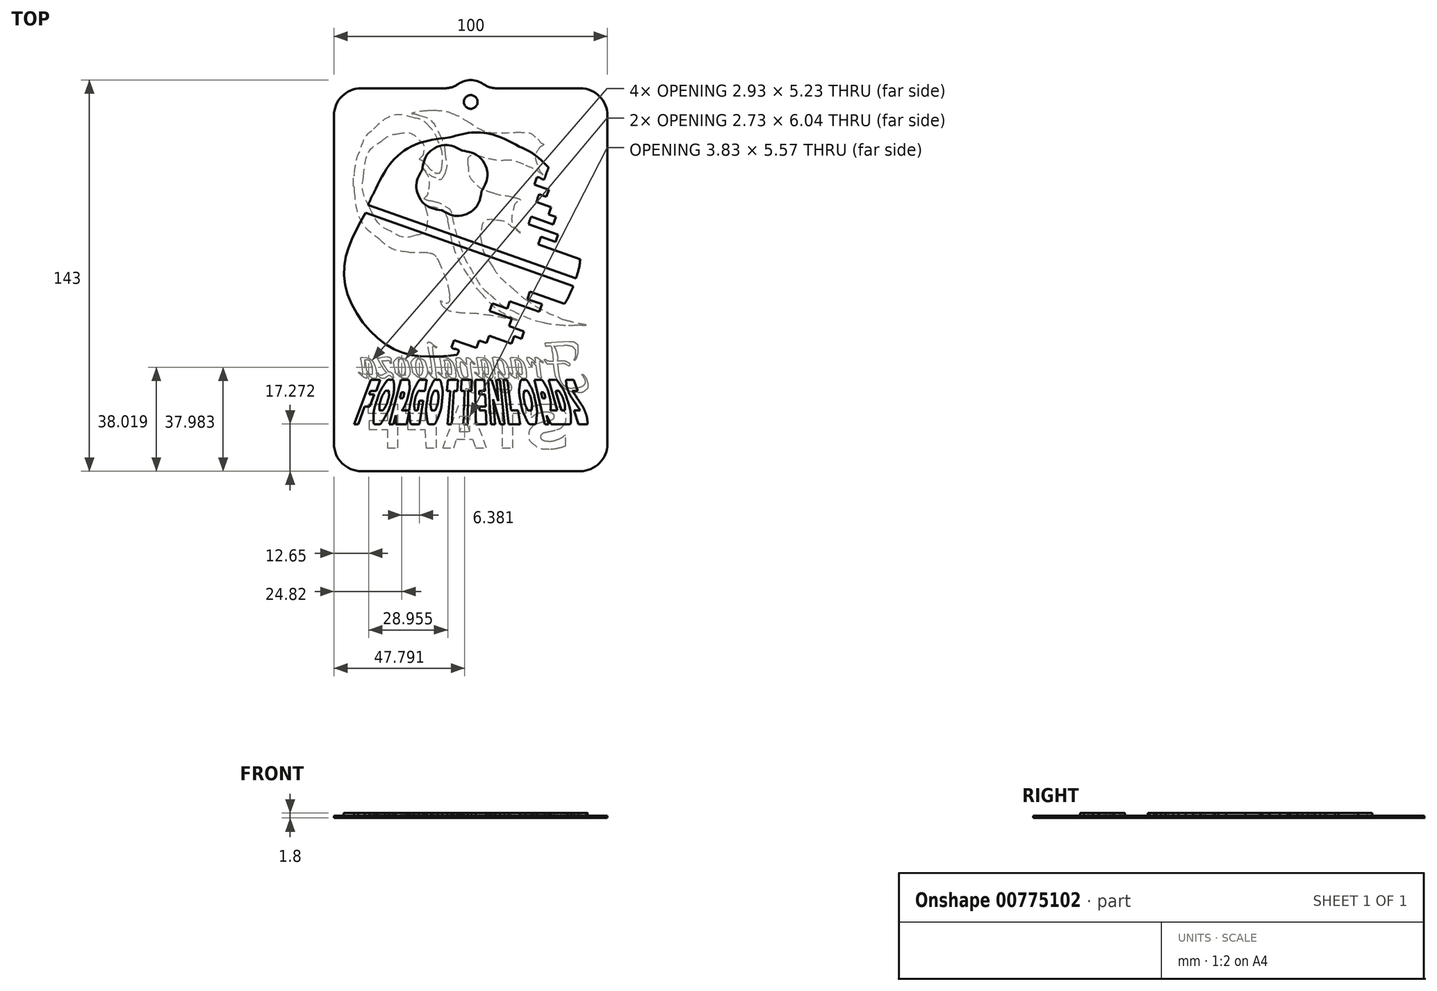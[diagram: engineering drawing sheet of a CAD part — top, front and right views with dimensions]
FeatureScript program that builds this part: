
annotation { "Feature Type Name" : "Feature", "Feature Type Description" : "" }
export const myFeature = defineFeature(function(context is Context, id is Id, definition is map)
    precondition{}
    {
        {
            var Q0;
            Q0=qCreatedBy(makeId("Top.planeOp"),FACE);
            var sketch = newSketch(context, id + "F0", { "sketchPlane" : qUnion([Q0])});
            skLineSegment(sketch, "E0.bottom", {"start": v(-40, 70) * mm, "end": v(-9.33, 70) * mm});
            skLineSegment(sketch, "E0.top", {"start": v(-40, -70) * mm, "end": v(40, -70) * mm});
            skLineSegment(sketch, "E0.left", {"start": v(-50, 60) * mm, "end": v(-50, -60) * mm});
            skLineSegment(sketch, "E0.right", {"start": v(50, 60) * mm, "end": v(50, -60) * mm});
            skPoint(sketch, "E0.middle", {"position": v(0, 0) * mm});
            skCircle(sketch, "E1", {"center": v(0, 65) * mm, "radius": 2.5 * mm});
            skPoint(sketch, "E2.visualSharp", {"position": v(-50, 70) * mm});
            skArc(sketch, "E2.filletArc", {"start": v(-40, 70) * mm, "mid": v(-47.07, 67.07) * mm, "end": v(-50, 60) * mm});
            skPoint(sketch, "E3.visualSharp", {"position": v(50, 70) * mm});
            skArc(sketch, "E3.filletArc", {"start": v(50, 60) * mm, "mid": v(47.07, 67.07) * mm, "end": v(40, 70) * mm});
            skPoint(sketch, "E4.visualSharp", {"position": v(50, -70) * mm});
            skArc(sketch, "E4.filletArc", {"start": v(40, -70) * mm, "mid": v(47.07, -67.07) * mm, "end": v(50, -60) * mm});
            skPoint(sketch, "E5.visualSharp", {"position": v(-50, -70) * mm});
            skArc(sketch, "E5.filletArc", {"start": v(-50, -60) * mm, "mid": v(-47.07, -67.07) * mm, "end": v(-40, -70) * mm});
            skArc(sketch, "E6", {"start": v(-4.66, 71.5) * mm, "mid": v(0, 73) * mm, "end": v(4.66, 71.5) * mm});
            skArc(sketch, "E7.filletArc", {"start": v(-9.33, 70) * mm, "mid": v(-6.88, 70.38) * mm, "end": v(-4.66, 71.5) * mm});
            skLineSegment(sketch, "E8", {"start": v(40, 70) * mm, "end": v(9.33, 70) * mm});
            skArc(sketch, "E9.filletArc", {"start": v(4.66, 71.5) * mm, "mid": v(6.88, 70.38) * mm, "end": v(9.33, 70) * mm});
            skSolve(sketch);
        }
        {
            var Q0;
            Q0=qCreatedBy(makeId("Top.planeOp"),FACE);
            var sketch = newSketch(context, id + "F1", { "sketchPlane" : qUnion([Q0])});
            skLineSegment(sketch, "E10", {"start": v(38.17, -16.7) * mm, "end": v(38.78, -16.7) * mm});
            skLineSegment(sketch, "E11", {"start": v(-13.07, 61.96) * mm, "end": v(-13.17, 61.96) * mm});
            skLineSegment(sketch, "E12", {"start": v(-14.17, 61.96) * mm, "end": v(-14.37, 61.96) * mm});
            skLineSegment(sketch, "E13", {"start": v(-42.85, 37.93) * mm, "end": v(-42.85, 36.81) * mm});
            skLineSegment(sketch, "E14", {"start": v(-42.85, 35.49) * mm, "end": v(-42.85, 34.98) * mm});
            skLineSegment(sketch, "E15", {"start": v(-42.85, 34.78) * mm, "end": v(-42.85, 34.16) * mm});
            skLineSegment(sketch, "E16", {"start": v(40.64, -16.7) * mm, "end": v(40.63, -16.62) * mm});
            skLineSegment(sketch, "E17", {"start": v(38.83, -16.7) * mm, "end": v(40.64, -16.7) * mm});
            skLineSegment(sketch, "E18", {"start": v(-42.85, 36.81) * mm, "end": v(-42.85, 35.49) * mm});
            skLineSegment(sketch, "E19", {"start": v(-13.21, 61.96) * mm, "end": v(-14.22, 61.96) * mm});
            skLineSegment(sketch, "E20", {"start": v(-42.85, 34.98) * mm, "end": v(-42.85, 34.77) * mm});
            skLineSegment(sketch, "E21", {"start": v(36.03, -31.52) * mm, "end": v(35.01, -30.98) * mm});
            skLineSegment(sketch, "E22", {"start": v(33.37, -30.7) * mm, "end": v(32.17, -30.75) * mm});
            skLineSegment(sketch, "E23", {"start": v(32.17, -30.75) * mm, "end": v(30.92, -30.82) * mm});
            skLineSegment(sketch, "E24", {"start": v(30.92, -30.82) * mm, "end": v(27.9, -30.82) * mm});
            skLineSegment(sketch, "E25", {"start": v(27.9, -30.82) * mm, "end": v(27.52, -30.26) * mm});
            skLineSegment(sketch, "E26", {"start": v(26.88, -29.35) * mm, "end": v(26.9, -29.28) * mm});
            skLineSegment(sketch, "E27", {"start": v(30.32, -29.76) * mm, "end": v(31.57, -29.76) * mm});
            skLineSegment(sketch, "E28", {"start": v(31.57, -29.76) * mm, "end": v(33.15, -29.76) * mm});
            skLineSegment(sketch, "E29", {"start": v(33.15, -29.76) * mm, "end": v(34.41, -29.76) * mm});
            skLineSegment(sketch, "E30", {"start": v(34.05, -24.06) * mm, "end": v(31.6, -24.16) * mm});
            skLineSegment(sketch, "E31", {"start": v(31.6, -24.16) * mm, "end": v(29.36, -24.3) * mm});
            skLineSegment(sketch, "E32", {"start": v(27.3, -24.39) * mm, "end": v(27.09, -23.13) * mm});
            skLineSegment(sketch, "E33", {"start": v(29.45, -22.97) * mm, "end": v(31.35, -22.93) * mm});
            skLineSegment(sketch, "E34", {"start": v(31.35, -22.93) * mm, "end": v(33.78, -22.78) * mm});
            skLineSegment(sketch, "E35", {"start": v(33.78, -22.78) * mm, "end": v(36.14, -22.66) * mm});
            skLineSegment(sketch, "E36", {"start": v(38.04, -29.5) * mm, "end": v(37.7, -29.32) * mm});
            skLineSegment(sketch, "E37", {"start": v(30.25, -30.2) * mm, "end": v(29.88, -26.54) * mm});
            skLineSegment(sketch, "E38", {"start": v(29.55, -24.56) * mm, "end": v(29.3, -24.3) * mm});
            skLineSegment(sketch, "E39", {"start": v(29.18, -23.96) * mm, "end": v(29.55, -24.04) * mm});
            skLineSegment(sketch, "E40", {"start": v(31.76, -29.06) * mm, "end": v(31.88, -31.82) * mm});
            skLineSegment(sketch, "E41", {"start": v(37.27, -39.71) * mm, "end": v(38.3, -39.63) * mm});
            skLineSegment(sketch, "E42", {"start": v(41.15, -35.4) * mm, "end": v(40.78, -34.92) * mm});
            skLineSegment(sketch, "E43", {"start": v(40.78, -34.92) * mm, "end": v(40.72, -34.76) * mm});
            skLineSegment(sketch, "E44", {"start": v(23.56, -29.53) * mm, "end": v(23.5, -28.89) * mm});
            skLineSegment(sketch, "E45", {"start": v(24.23, -28.54) * mm, "end": v(25.22, -29.23) * mm});
            skLineSegment(sketch, "E46", {"start": v(25.22, -29.23) * mm, "end": v(26.33, -30.01) * mm});
            skLineSegment(sketch, "E47", {"start": v(26.48, -30.3) * mm, "end": v(26.4, -30.34) * mm});
            skLineSegment(sketch, "E48", {"start": v(26.4, -30.34) * mm, "end": v(26.3, -30.32) * mm});
            skLineSegment(sketch, "E49", {"start": v(26.3, -30.32) * mm, "end": v(26.17, -30.3) * mm});
            skLineSegment(sketch, "E50", {"start": v(25.15, -30.3) * mm, "end": v(25.53, -33.54) * mm});
            skLineSegment(sketch, "E51", {"start": v(25.53, -33.54) * mm, "end": v(25.79, -35.64) * mm});
            skLineSegment(sketch, "E52", {"start": v(25.88, -36) * mm, "end": v(24.4, -35.44) * mm});
            skLineSegment(sketch, "E53", {"start": v(23.19, -29.85) * mm, "end": v(23.89, -30.75) * mm});
            skLineSegment(sketch, "E54", {"start": v(23.65, -31.18) * mm, "end": v(23.19, -30.77) * mm});
            skLineSegment(sketch, "E55", {"start": v(15.9, -29.4) * mm, "end": v(15.4, -29.4) * mm});
            skLineSegment(sketch, "E56", {"start": v(15.4, -29.4) * mm, "end": v(15.02, -29.33) * mm});
            skLineSegment(sketch, "E57", {"start": v(15.24, -28.42) * mm, "end": v(16.71, -28.55) * mm});
            skLineSegment(sketch, "E58", {"start": v(17.3, -34.56) * mm, "end": v(16.63, -33.84) * mm});
            skLineSegment(sketch, "E59", {"start": v(16.01, -32.3) * mm, "end": v(16.46, -32.84) * mm});
            skLineSegment(sketch, "E60", {"start": v(16.96, -29.4) * mm, "end": v(16.5, -29.4) * mm});
            skLineSegment(sketch, "E61", {"start": v(16.5, -29.4) * mm, "end": v(15.9, -29.4) * mm});
            skLineSegment(sketch, "E62", {"start": v(16.38, -31.1) * mm, "end": v(16.6, -32.79) * mm});
            skLineSegment(sketch, "E63", {"start": v(16.6, -32.79) * mm, "end": v(16.8, -34.4) * mm});
            skLineSegment(sketch, "E64", {"start": v(16.8, -34.4) * mm, "end": v(16.85, -35.3) * mm});
            skLineSegment(sketch, "E65", {"start": v(14.85, -34.45) * mm, "end": v(15.26, -34.75) * mm});
            skLineSegment(sketch, "E66", {"start": v(15.33, -34.51) * mm, "end": v(15.26, -33.72) * mm});
            skLineSegment(sketch, "E67", {"start": v(15.26, -33.72) * mm, "end": v(14.93, -31.64) * mm});
            skLineSegment(sketch, "E68", {"start": v(14.93, -31.64) * mm, "end": v(14.54, -29.14) * mm});
            skLineSegment(sketch, "E69", {"start": v(9.13, -29.4) * mm, "end": v(8.63, -29.4) * mm});
            skLineSegment(sketch, "E70", {"start": v(8.63, -29.4) * mm, "end": v(8.27, -29.31) * mm});
            skLineSegment(sketch, "E71", {"start": v(8.04, -29.08) * mm, "end": v(7.89, -28.74) * mm});
            skLineSegment(sketch, "E72", {"start": v(8.47, -28.35) * mm, "end": v(8.95, -28.35) * mm});
            skLineSegment(sketch, "E73", {"start": v(8.95, -28.35) * mm, "end": v(9.46, -28.52) * mm});
            skLineSegment(sketch, "E74", {"start": v(9.46, -28.52) * mm, "end": v(10.14, -28.6) * mm});
            skLineSegment(sketch, "E75", {"start": v(11.28, -34.74) * mm, "end": v(10.47, -33.88) * mm});
            skLineSegment(sketch, "E76", {"start": v(9.69, -32.05) * mm, "end": v(10.37, -32.95) * mm});
            skLineSegment(sketch, "E77", {"start": v(10.37, -32.95) * mm, "end": v(11.14, -33.94) * mm});
            skLineSegment(sketch, "E78", {"start": v(12.6, -34.13) * mm, "end": v(12.52, -33.32) * mm});
            skLineSegment(sketch, "E79", {"start": v(12.52, -33.32) * mm, "end": v(12.29, -32.26) * mm});
            skLineSegment(sketch, "E80", {"start": v(12.29, -32.26) * mm, "end": v(12.13, -31.6) * mm});
            skLineSegment(sketch, "E81", {"start": v(10.33, -29.4) * mm, "end": v(9.77, -29.4) * mm});
            skLineSegment(sketch, "E82", {"start": v(9.77, -29.4) * mm, "end": v(9.13, -29.4) * mm});
            skLineSegment(sketch, "E83", {"start": v(9.46, -28.84) * mm, "end": v(9.77, -30.97) * mm});
            skLineSegment(sketch, "E84", {"start": v(9.77, -30.97) * mm, "end": v(10.1, -34.04) * mm});
            skLineSegment(sketch, "E85", {"start": v(10.1, -34.04) * mm, "end": v(10.34, -36.29) * mm});
            skLineSegment(sketch, "E86", {"start": v(10.34, -36.29) * mm, "end": v(10.47, -37.68) * mm});
            skLineSegment(sketch, "E87", {"start": v(12.25, -36.7) * mm, "end": v(11.22, -36.28) * mm});
            skLineSegment(sketch, "E88", {"start": v(10.66, -36) * mm, "end": v(10.7, -35.94) * mm});
            skLineSegment(sketch, "E89", {"start": v(8.88, -35.3) * mm, "end": v(8.5, -31.75) * mm});
            skLineSegment(sketch, "E90", {"start": v(3.54, -29.4) * mm, "end": v(3.04, -29.4) * mm});
            skLineSegment(sketch, "E91", {"start": v(3.04, -29.4) * mm, "end": v(2.67, -29.33) * mm});
            skLineSegment(sketch, "E92", {"start": v(2.88, -28.42) * mm, "end": v(4.36, -28.55) * mm});
            skLineSegment(sketch, "E93", {"start": v(4.94, -34.56) * mm, "end": v(4.28, -33.84) * mm});
            skLineSegment(sketch, "E94", {"start": v(3.66, -32.3) * mm, "end": v(4.1, -32.84) * mm});
            skLineSegment(sketch, "E95", {"start": v(4.6, -29.4) * mm, "end": v(4.14, -29.4) * mm});
            skLineSegment(sketch, "E96", {"start": v(4.14, -29.4) * mm, "end": v(3.54, -29.4) * mm});
            skLineSegment(sketch, "E97", {"start": v(4.02, -31.1) * mm, "end": v(4.25, -32.79) * mm});
            skLineSegment(sketch, "E98", {"start": v(4.25, -32.79) * mm, "end": v(4.44, -34.4) * mm});
            skLineSegment(sketch, "E99", {"start": v(4.44, -34.4) * mm, "end": v(4.5, -35.3) * mm});
            skLineSegment(sketch, "E100", {"start": v(2.5, -34.45) * mm, "end": v(2.9, -34.75) * mm});
            skLineSegment(sketch, "E101", {"start": v(2.98, -34.51) * mm, "end": v(2.9, -33.72) * mm});
            skLineSegment(sketch, "E102", {"start": v(2.9, -33.72) * mm, "end": v(2.58, -31.64) * mm});
            skLineSegment(sketch, "E103", {"start": v(2.58, -31.64) * mm, "end": v(2.19, -29.14) * mm});
            skLineSegment(sketch, "E104", {"start": v(-0.07, -30.77) * mm, "end": v(0.03, -32.01) * mm});
            skLineSegment(sketch, "E105", {"start": v(0.03, -32.01) * mm, "end": v(0.35, -34.14) * mm});
            skLineSegment(sketch, "E106", {"start": v(0.35, -34.14) * mm, "end": v(0.85, -37.11) * mm});
            skLineSegment(sketch, "E107", {"start": v(0.96, -41.4) * mm, "end": v(0.32, -41.16) * mm});
            skLineSegment(sketch, "E108", {"start": v(-0.43, -39.67) * mm, "end": v(-0.47, -38.83) * mm});
            skLineSegment(sketch, "E109", {"start": v(-0.47, -38.83) * mm, "end": v(-0.77, -36.7) * mm});
            skLineSegment(sketch, "E110", {"start": v(-0.77, -36.7) * mm, "end": v(-1.14, -33.74) * mm});
            skLineSegment(sketch, "E111", {"start": v(-1.14, -33.74) * mm, "end": v(-1.34, -32.16) * mm});
            skLineSegment(sketch, "E112", {"start": v(-1.34, -32.16) * mm, "end": v(-1.56, -30.34) * mm});
            skLineSegment(sketch, "E113", {"start": v(-1.56, -30.34) * mm, "end": v(-1.62, -29.37) * mm});
            skLineSegment(sketch, "E114", {"start": v(-0.41, -35.45) * mm, "end": v(-0.36, -35.65) * mm});
            skLineSegment(sketch, "E115", {"start": v(-0.18, -36.1) * mm, "end": v(-0.24, -36.16) * mm});
            skLineSegment(sketch, "E116", {"start": v(-0.24, -36.16) * mm, "end": v(-0.31, -36.19) * mm});
            skLineSegment(sketch, "E117", {"start": v(-0.31, -36.19) * mm, "end": v(-0.7, -36.11) * mm});
            skLineSegment(sketch, "E118", {"start": v(-0.7, -36.11) * mm, "end": v(-1.4, -36.11) * mm});
            skLineSegment(sketch, "E119", {"start": v(-1.4, -36.11) * mm, "end": v(-2.27, -36.11) * mm});
            skLineSegment(sketch, "E120", {"start": v(-2.53, -30.03) * mm, "end": v(-1.85, -30.67) * mm});
            skLineSegment(sketch, "E121", {"start": v(-9.94, -29.4) * mm, "end": v(-10.44, -29.4) * mm});
            skLineSegment(sketch, "E122", {"start": v(-10.44, -29.4) * mm, "end": v(-10.8, -29.33) * mm});
            skLineSegment(sketch, "E123", {"start": v(-10.6, -28.42) * mm, "end": v(-9.12, -28.55) * mm});
            skLineSegment(sketch, "E124", {"start": v(-8.54, -34.56) * mm, "end": v(-9.2, -33.84) * mm});
            skLineSegment(sketch, "E125", {"start": v(-9.82, -32.3) * mm, "end": v(-9.37, -32.84) * mm});
            skLineSegment(sketch, "E126", {"start": v(-8.87, -29.4) * mm, "end": v(-9.34, -29.4) * mm});
            skLineSegment(sketch, "E127", {"start": v(-9.34, -29.4) * mm, "end": v(-9.94, -29.4) * mm});
            skLineSegment(sketch, "E128", {"start": v(-9.46, -31.1) * mm, "end": v(-9.23, -32.79) * mm});
            skLineSegment(sketch, "E129", {"start": v(-9.23, -32.79) * mm, "end": v(-9.04, -34.4) * mm});
            skLineSegment(sketch, "E130", {"start": v(-9.04, -34.4) * mm, "end": v(-8.99, -35.3) * mm});
            skLineSegment(sketch, "E131", {"start": v(-10.98, -34.45) * mm, "end": v(-10.58, -34.75) * mm});
            skLineSegment(sketch, "E132", {"start": v(-10.5, -34.51) * mm, "end": v(-10.58, -33.72) * mm});
            skLineSegment(sketch, "E133", {"start": v(-10.58, -33.72) * mm, "end": v(-10.9, -31.64) * mm});
            skLineSegment(sketch, "E134", {"start": v(-10.9, -31.64) * mm, "end": v(-11.29, -29.14) * mm});
            skLineSegment(sketch, "E135", {"start": v(-14.16, -33.74) * mm, "end": v(-14.26, -32.52) * mm});
            skLineSegment(sketch, "E136", {"start": v(-14.26, -32.52) * mm, "end": v(-14.56, -30.46) * mm});
            skLineSegment(sketch, "E137", {"start": v(-14.56, -30.46) * mm, "end": v(-15.08, -27.43) * mm});
            skLineSegment(sketch, "E138", {"start": v(-15, -22.92) * mm, "end": v(-14.03, -23.56) * mm});
            skLineSegment(sketch, "E139", {"start": v(-12.63, -24.87) * mm, "end": v(-12.86, -24.8) * mm});
            skLineSegment(sketch, "E140", {"start": v(-13.91, -24.76) * mm, "end": v(-13.85, -25.5) * mm});
            skLineSegment(sketch, "E141", {"start": v(-13.85, -25.5) * mm, "end": v(-13.65, -26.9) * mm});
            skLineSegment(sketch, "E142", {"start": v(-13.65, -26.9) * mm, "end": v(-13.36, -28.73) * mm});
            skLineSegment(sketch, "E143", {"start": v(-13.36, -28.73) * mm, "end": v(-13.08, -30.79) * mm});
            skLineSegment(sketch, "E144", {"start": v(-13.08, -30.79) * mm, "end": v(-12.8, -32.84) * mm});
            skLineSegment(sketch, "E145", {"start": v(-12.8, -32.84) * mm, "end": v(-12.61, -34.45) * mm});
            skLineSegment(sketch, "E146", {"start": v(-12.61, -34.45) * mm, "end": v(-12.55, -35.39) * mm});
            skLineSegment(sketch, "E147", {"start": v(-19.13, -35.54) * mm, "end": v(-20.12, -34.9) * mm});
            skLineSegment(sketch, "E148", {"start": v(-21.26, -33.55) * mm, "end": v(-21.5, -32.5) * mm});
            skLineSegment(sketch, "E149", {"start": v(-21.5, -32.5) * mm, "end": v(-21.73, -31.52) * mm});
            skLineSegment(sketch, "E150", {"start": v(-21.73, -31.52) * mm, "end": v(-21.79, -30.84) * mm});
            skLineSegment(sketch, "E151", {"start": v(-19.8, -28.37) * mm, "end": v(-19.36, -28.42) * mm});
            skLineSegment(sketch, "E152", {"start": v(-19.36, -28.42) * mm, "end": v(-18.37, -28.75) * mm});
            skLineSegment(sketch, "E153", {"start": v(-17.54, -31.66) * mm, "end": v(-18, -30.05) * mm});
            skLineSegment(sketch, "E154", {"start": v(-25.5, -35.54) * mm, "end": v(-26.5, -34.9) * mm});
            skLineSegment(sketch, "E155", {"start": v(-27.64, -33.55) * mm, "end": v(-27.88, -32.5) * mm});
            skLineSegment(sketch, "E156", {"start": v(-27.88, -32.5) * mm, "end": v(-28.1, -31.52) * mm});
            skLineSegment(sketch, "E157", {"start": v(-28.1, -31.52) * mm, "end": v(-28.17, -30.84) * mm});
            skLineSegment(sketch, "E158", {"start": v(-26.19, -28.37) * mm, "end": v(-25.74, -28.42) * mm});
            skLineSegment(sketch, "E159", {"start": v(-25.74, -28.42) * mm, "end": v(-24.75, -28.75) * mm});
            skLineSegment(sketch, "E160", {"start": v(-23.92, -31.66) * mm, "end": v(-24.38, -30.05) * mm});
            skLineSegment(sketch, "E161", {"start": v(-30.82, -29.63) * mm, "end": v(-31.6, -29.66) * mm});
            skLineSegment(sketch, "E162", {"start": v(-31.6, -29.66) * mm, "end": v(-32.28, -29.63) * mm});
            skLineSegment(sketch, "E163", {"start": v(-32.28, -29.63) * mm, "end": v(-32.6, -29.59) * mm});
            skLineSegment(sketch, "E164", {"start": v(-28.05, -35.7) * mm, "end": v(-28.34, -36) * mm});
            skLineSegment(sketch, "E165", {"start": v(-32.16, -32.19) * mm, "end": v(-32.67, -31.4) * mm});
            skLineSegment(sketch, "E166", {"start": v(-32.67, -31.4) * mm, "end": v(-33.23, -30.44) * mm});
            skLineSegment(sketch, "E167", {"start": v(-33.23, -30.44) * mm, "end": v(-33.8, -29.45) * mm});
            skLineSegment(sketch, "E168", {"start": v(-33.8, -29.45) * mm, "end": v(-34.28, -28.64) * mm});
            skLineSegment(sketch, "E169", {"start": v(-34.18, -28.33) * mm, "end": v(-34.02, -28.38) * mm});
            skLineSegment(sketch, "E170", {"start": v(-33.17, -28.56) * mm, "end": v(-32.43, -28.52) * mm});
            skLineSegment(sketch, "E171", {"start": v(-32.43, -28.52) * mm, "end": v(-31.52, -28.4) * mm});
            skLineSegment(sketch, "E172", {"start": v(-31.52, -28.4) * mm, "end": v(-30.4, -28.23) * mm});
            skLineSegment(sketch, "E173", {"start": v(-29.1, -29.33) * mm, "end": v(-29.02, -30) * mm});
            skLineSegment(sketch, "E174", {"start": v(-28.09, -35.68) * mm, "end": v(-28.22, -35.85) * mm});
            skLineSegment(sketch, "E175", {"start": v(-28.4, -35.95) * mm, "end": v(-29.27, -35.27) * mm});
            skLineSegment(sketch, "E176", {"start": v(-32.12, -34.67) * mm, "end": v(-31.13, -34.22) * mm});
            skLineSegment(sketch, "E177", {"start": v(-31.13, -34.22) * mm, "end": v(-30.22, -33.8) * mm});
            skLineSegment(sketch, "E178", {"start": v(-28.36, -35.08) * mm, "end": v(-28.32, -35.29) * mm});
            skLineSegment(sketch, "E179", {"start": v(-28.32, -35.29) * mm, "end": v(-28.26, -35.48) * mm});
            skLineSegment(sketch, "E180", {"start": v(-28.26, -35.48) * mm, "end": v(-28.09, -35.68) * mm});
            skLineSegment(sketch, "E181", {"start": v(-38.9, -29.4) * mm, "end": v(-39.4, -29.4) * mm});
            skLineSegment(sketch, "E182", {"start": v(-39.4, -29.4) * mm, "end": v(-39.76, -29.33) * mm});
            skLineSegment(sketch, "E183", {"start": v(-39.55, -28.42) * mm, "end": v(-38.08, -28.55) * mm});
            skLineSegment(sketch, "E184", {"start": v(-37.5, -34.56) * mm, "end": v(-38.15, -33.84) * mm});
            skLineSegment(sketch, "E185", {"start": v(-38.77, -32.3) * mm, "end": v(-38.33, -32.84) * mm});
            skLineSegment(sketch, "E186", {"start": v(-37.82, -29.4) * mm, "end": v(-38.3, -29.4) * mm});
            skLineSegment(sketch, "E187", {"start": v(-38.3, -29.4) * mm, "end": v(-38.9, -29.4) * mm});
            skLineSegment(sketch, "E188", {"start": v(-38.41, -31.1) * mm, "end": v(-38.19, -32.79) * mm});
            skLineSegment(sketch, "E189", {"start": v(-38.19, -32.79) * mm, "end": v(-38, -34.4) * mm});
            skLineSegment(sketch, "E190", {"start": v(-38, -34.4) * mm, "end": v(-37.94, -35.3) * mm});
            skLineSegment(sketch, "E191", {"start": v(-39.94, -34.45) * mm, "end": v(-39.53, -34.75) * mm});
            skLineSegment(sketch, "E192", {"start": v(-39.45, -34.51) * mm, "end": v(-39.53, -33.72) * mm});
            skLineSegment(sketch, "E193", {"start": v(-39.53, -33.72) * mm, "end": v(-39.86, -31.64) * mm});
            skLineSegment(sketch, "E194", {"start": v(-39.86, -31.64) * mm, "end": v(-40.24, -29.14) * mm});
            skLineSegment(sketch, "E195", {"start": v(22.49, -50.22) * mm, "end": v(22.06, -50.22) * mm});
            skLineSegment(sketch, "E196", {"start": v(22.06, -50.22) * mm, "end": v(22.06, -46.56) * mm});
            skLineSegment(sketch, "E197", {"start": v(34.32, -56.92) * mm, "end": v(34.76, -56.92) * mm});
            skLineSegment(sketch, "E198", {"start": v(34.76, -56.92) * mm, "end": v(34.76, -60.73) * mm});
            skLineSegment(sketch, "E199", {"start": v(6.54, -45.64) * mm, "end": v(20.3, -45.64) * mm});
            skLineSegment(sketch, "E200", {"start": v(20.3, -45.64) * mm, "end": v(20.3, -48.81) * mm});
            skLineSegment(sketch, "E201", {"start": v(20.3, -48.81) * mm, "end": v(15.36, -48.81) * mm});
            skLineSegment(sketch, "E202", {"start": v(15.36, -48.81) * mm, "end": v(15.36, -61.51) * mm});
            skLineSegment(sketch, "E203", {"start": v(15.36, -61.51) * mm, "end": v(11.47, -61.51) * mm});
            skLineSegment(sketch, "E204", {"start": v(11.47, -61.51) * mm, "end": v(11.47, -48.81) * mm});
            skLineSegment(sketch, "E205", {"start": v(11.47, -48.81) * mm, "end": v(6.54, -48.81) * mm});
            skLineSegment(sketch, "E206", {"start": v(6.54, -48.81) * mm, "end": v(6.54, -45.64) * mm});
            skLineSegment(sketch, "E207", {"start": v(-4.56, -45.99) * mm, "end": v(0.04, -45.99) * mm});
            skLineSegment(sketch, "E208", {"start": v(0.04, -45.99) * mm, "end": v(5.78, -61.51) * mm});
            skLineSegment(sketch, "E209", {"start": v(5.78, -61.51) * mm, "end": v(1.8, -61.51) * mm});
            skLineSegment(sketch, "E210", {"start": v(1.8, -61.51) * mm, "end": v(0.7, -58.34) * mm});
            skLineSegment(sketch, "E211", {"start": v(0.7, -58.34) * mm, "end": v(-5.12, -58.34) * mm});
            skLineSegment(sketch, "E212", {"start": v(-5.12, -58.34) * mm, "end": v(-6.2, -61.51) * mm});
            skLineSegment(sketch, "E213", {"start": v(-6.2, -61.51) * mm, "end": v(-10.3, -61.51) * mm});
            skLineSegment(sketch, "E214", {"start": v(-10.3, -61.51) * mm, "end": v(-4.56, -45.99) * mm});
            skLineSegment(sketch, "E215", {"start": v(-0.3, -55.51) * mm, "end": v(-2.2, -49.94) * mm});
            skLineSegment(sketch, "E216", {"start": v(-2.2, -49.94) * mm, "end": v(-4.12, -55.51) * mm});
            skLineSegment(sketch, "E217", {"start": v(-4.12, -55.51) * mm, "end": v(-0.3, -55.51) * mm});
            skLineSegment(sketch, "E218", {"start": v(-23.8, -45.64) * mm, "end": v(-12.51, -45.64) * mm});
            skLineSegment(sketch, "E219", {"start": v(-12.51, -45.64) * mm, "end": v(-12.51, -61.51) * mm});
            skLineSegment(sketch, "E220", {"start": v(-12.51, -61.51) * mm, "end": v(-16.4, -61.51) * mm});
            skLineSegment(sketch, "E221", {"start": v(-16.4, -61.51) * mm, "end": v(-16.75, -54.8) * mm});
            skLineSegment(sketch, "E222", {"start": v(-16.75, -54.8) * mm, "end": v(-23.1, -54.8) * mm});
            skLineSegment(sketch, "E223", {"start": v(-23.1, -54.8) * mm, "end": v(-23.1, -51.63) * mm});
            skLineSegment(sketch, "E224", {"start": v(-23.1, -51.63) * mm, "end": v(-16.75, -51.63) * mm});
            skLineSegment(sketch, "E225", {"start": v(-16.75, -51.63) * mm, "end": v(-16.75, -48.81) * mm});
            skLineSegment(sketch, "E226", {"start": v(-16.75, -48.81) * mm, "end": v(-23.8, -48.81) * mm});
            skLineSegment(sketch, "E227", {"start": v(-23.8, -48.81) * mm, "end": v(-23.8, -45.64) * mm});
            skLineSegment(sketch, "E228", {"start": v(-37.56, -45.64) * mm, "end": v(-26.63, -45.64) * mm});
            skLineSegment(sketch, "E229", {"start": v(-26.63, -45.64) * mm, "end": v(-26.63, -61.51) * mm});
            skLineSegment(sketch, "E230", {"start": v(-26.63, -61.51) * mm, "end": v(-30.5, -61.51) * mm});
            skLineSegment(sketch, "E231", {"start": v(-30.5, -61.51) * mm, "end": v(-30.5, -54.8) * mm});
            skLineSegment(sketch, "E232", {"start": v(-30.5, -54.8) * mm, "end": v(-37.2, -54.8) * mm});
            skLineSegment(sketch, "E233", {"start": v(-37.2, -54.8) * mm, "end": v(-37.2, -51.63) * mm});
            skLineSegment(sketch, "E234", {"start": v(-37.2, -51.63) * mm, "end": v(-30.5, -51.63) * mm});
            skLineSegment(sketch, "E235", {"start": v(-30.5, -51.63) * mm, "end": v(-30.5, -48.81) * mm});
            skLineSegment(sketch, "E236", {"start": v(-30.5, -48.81) * mm, "end": v(-37.56, -48.81) * mm});
            skLineSegment(sketch, "E237", {"start": v(-37.56, -48.81) * mm, "end": v(-37.56, -45.64) * mm});
            skFitSpline(sketch, "E238", {"points": [v(-14.37, 61.96) * mm, v(-14.8, 61.78) * mm, v(-15.26, 61.8) * mm, v(-15.71, 61.76) * mm]});
            skFitSpline(sketch, "E239", {"points": [v(-15.71, 61.76) * mm, v(-17.53, 61.62) * mm, v(-19.32, 61.38) * mm, v(-21.1, 60.93) * mm]});
            skFitSpline(sketch, "E240", {"points": [v(-21.1, 60.93) * mm, v(-21.24, 60.9) * mm, v(-21.43, 60.9) * mm, v(-21.54, 60.66) * mm]});
            skFitSpline(sketch, "E241", {"points": [v(-21.54, 60.66) * mm, v(-20.54, 60.63) * mm, v(-19.62, 60.35) * mm, v(-18.7, 60.03) * mm]});
            skFitSpline(sketch, "E242", {"points": [v(-18.7, 60.03) * mm, v(-15.38, 58.87) * mm, v(-13.15, 56.52) * mm, v(-11.58, 53.44) * mm]});
            skFitSpline(sketch, "E243", {"points": [v(-11.58, 53.44) * mm, v(-10.47, 51.29) * mm, v(-9.71, 49) * mm, v(-9.41, 46.6) * mm]});
            skFitSpline(sketch, "E244", {"points": [v(-9.41, 46.6) * mm, v(-9.11, 44.15) * mm, v(-8.77, 41.68) * mm, v(-9.35, 39.2) * mm]});
            skFitSpline(sketch, "E245", {"points": [v(-9.35, 39.2) * mm, v(-9.4, 38.94) * mm, v(-9.5, 38.7) * mm, v(-9.63, 38.47) * mm]});
            skFitSpline(sketch, "E246", {"points": [v(-9.63, 38.47) * mm, v(-10.22, 37.39) * mm, v(-11.1, 36.57) * mm, v(-12.72, 37.2) * mm]});
            skFitSpline(sketch, "E247", {"points": [v(-12.72, 37.2) * mm, v(-14.12, 37.75) * mm, v(-15.28, 38.64) * mm, v(-16.36, 39.65) * mm]});
            skFitSpline(sketch, "E248", {"points": [v(-16.36, 39.65) * mm, v(-16.66, 39.92) * mm, v(-16.91, 40.23) * mm, v(-17.25, 40.59) * mm]});
            skFitSpline(sketch, "E249", {"points": [v(-17.25, 40.59) * mm, v(-17.26, 40.3) * mm, v(-17.11, 40.19) * mm, v(-17.03, 40.05) * mm]});
            skFitSpline(sketch, "E250", {"points": [v(-17.03, 40.05) * mm, v(-15.47, 37.53) * mm, v(-15.17, 34.78) * mm, v(-15.68, 31.91) * mm]});
            skFitSpline(sketch, "E251", {"points": [v(-15.68, 31.91) * mm, v(-15.8, 31.24) * mm, v(-16.1, 30.64) * mm, v(-16.6, 30.16) * mm]});
            skFitSpline(sketch, "E252", {"points": [v(-16.6, 30.16) * mm, v(-17.12, 29.67) * mm, v(-17.1, 29.65) * mm, v(-16.44, 29.37) * mm]});
            skFitSpline(sketch, "E253", {"points": [v(-16.44, 29.37) * mm, v(-15.51, 28.97) * mm, v(-14.51, 28.87) * mm, v(-13.54, 28.62) * mm]});
            skFitSpline(sketch, "E254", {"points": [v(-13.54, 28.62) * mm, v(-11.87, 28.2) * mm, v(-10.3, 27.56) * mm, v(-8.86, 26.56) * mm]});
            skFitSpline(sketch, "E255", {"points": [v(-8.86, 26.56) * mm, v(-7.66, 25.72) * mm, v(-7.05, 24.5) * mm, v(-6.77, 23.12) * mm]});
            skFitSpline(sketch, "E256", {"points": [v(-6.77, 23.12) * mm, v(-6.07, 19.68) * mm, v(-5.15, 16.3) * mm, v(-4.03, 13) * mm]});
            skFitSpline(sketch, "E257", {"points": [v(-4.03, 13) * mm, v(-3.06, 10.12) * mm, v(-1.94, 7.3) * mm, v(-0.43, 4.69) * mm]});
            skFitSpline(sketch, "E258", {"points": [v(-0.43, 4.69) * mm, v(1.68, 1.04) * mm, v(3.89, -2.54) * mm, v(7.02, -5.42) * mm]});
            skFitSpline(sketch, "E259", {"points": [v(7.02, -5.42) * mm, v(9.48, -7.68) * mm, v(12.02, -9.8) * mm, v(15.04, -11.25) * mm]});
            skFitSpline(sketch, "E260", {"points": [v(15.04, -11.25) * mm, v(18.76, -13.03) * mm, v(22.58, -14.59) * mm, v(26.59, -15.61) * mm]});
            skFitSpline(sketch, "E261", {"points": [v(26.59, -15.61) * mm, v(28.25, -16.04) * mm, v(29.96, -16.23) * mm, v(31.67, -16.4) * mm]});
            skFitSpline(sketch, "E262", {"points": [v(31.67, -16.4) * mm, v(33.03, -16.54) * mm, v(34.4, -16.62) * mm, v(35.77, -16.62) * mm]});
            skFitSpline(sketch, "E263", {"points": [v(35.77, -16.62) * mm, v(36.22, -16.7) * mm, v(36.67, -16.64) * mm, v(37.13, -16.66) * mm]});
            skFitSpline(sketch, "E264", {"points": [v(37.13, -16.66) * mm, v(37.48, -16.68) * mm, v(37.83, -16.6) * mm, v(38.17, -16.7) * mm]});
            skFitSpline(sketch, "E265", {"points": [v(38.78, -16.7) * mm, v(39.38, -16.6) * mm, v(39.99, -16.69) * mm, v(40.59, -16.66) * mm]});
            skFitSpline(sketch, "E266", {"points": [v(40.59, -16.66) * mm, v(41.03, -16.65) * mm, v(41.48, -16.66) * mm, v(41.92, -16.65) * mm]});
            skFitSpline(sketch, "E267", {"points": [v(41.92, -16.65) * mm, v(42.02, -16.65) * mm, v(42.17, -16.71) * mm, v(42.18, -16.52) * mm]});
            skFitSpline(sketch, "E268", {"points": [v(42.18, -16.52) * mm, v(40.35, -16.18) * mm, v(38.52, -15.83) * mm, v(36.71, -15.35) * mm]});
            skFitSpline(sketch, "E269", {"points": [v(36.71, -15.35) * mm, v(36, -15.16) * mm, v(35.25, -15.03) * mm, v(34.53, -14.82) * mm]});
            skFitSpline(sketch, "E270", {"points": [v(34.53, -14.82) * mm, v(33.1, -14.38) * mm, v(31.81, -13.6) * mm, v(30.4, -13.1) * mm]});
            skFitSpline(sketch, "E271", {"points": [v(30.4, -13.1) * mm, v(28.9, -12.57) * mm, v(27.54, -11.75) * mm, v(26.13, -11.04) * mm]});
            skFitSpline(sketch, "E272", {"points": [v(26.13, -11.04) * mm, v(24.28, -10.1) * mm, v(22.61, -8.9) * mm, v(20.9, -7.78) * mm]});
            skFitSpline(sketch, "E273", {"points": [v(20.9, -7.78) * mm, v(19.32, -6.73) * mm, v(17.87, -5.46) * mm, v(16.43, -4.2) * mm]});
            skFitSpline(sketch, "E274", {"points": [v(16.43, -4.2) * mm, v(13.43, -1.57) * mm, v(10.5, 1.14) * mm, v(8.29, 4.51) * mm]});
            skFitSpline(sketch, "E275", {"points": [v(8.29, 4.51) * mm, v(6.39, 7.4) * mm, v(4.75, 10.42) * mm, v(4.04, 13.87) * mm]});
            skFitSpline(sketch, "E276", {"points": [v(4.04, 13.87) * mm, v(3.74, 15.29) * mm, v(3.6, 16.77) * mm, v(3.96, 18.15) * mm]});
            skFitSpline(sketch, "E277", {"points": [v(3.96, 18.15) * mm, v(4.68, 20.94) * mm, v(6.59, 22.1) * mm, v(9.37, 21.76) * mm]});
            skFitSpline(sketch, "E278", {"points": [v(9.37, 21.76) * mm, v(12.14, 21.42) * mm, v(14.36, 19.9) * mm, v(16.53, 18.28) * mm]});
            skFitSpline(sketch, "E279", {"points": [v(16.53, 18.28) * mm, v(17.05, 17.9) * mm, v(17.55, 17.5) * mm, v(18.06, 17.1) * mm]});
            skFitSpline(sketch, "E280", {"points": [v(18.06, 17.1) * mm, v(18.14, 17.24) * mm, v(18.06, 17.27) * mm, v(18.02, 17.3) * mm]});
            skFitSpline(sketch, "E281", {"points": [v(18.02, 17.3) * mm, v(15.67, 19.8) * mm, v(15.1, 22.76) * mm, v(15.81, 26.03) * mm]});
            skFitSpline(sketch, "E282", {"points": [v(15.81, 26.03) * mm, v(16.12, 27.45) * mm, v(16.96, 28.48) * mm, v(18.36, 29.08) * mm]});
            skFitSpline(sketch, "E283", {"points": [v(18.36, 29.08) * mm, v(17.45, 29.57) * mm, v(16.52, 29.83) * mm, v(15.58, 30.04) * mm]});
            skFitSpline(sketch, "E284", {"points": [v(15.58, 30.04) * mm, v(13.22, 30.57) * mm, v(10.83, 30.9) * mm, v(8.5, 31.57) * mm]});
            skFitSpline(sketch, "E285", {"points": [v(8.5, 31.57) * mm, v(7.27, 31.92) * mm, v(6.07, 32.36) * mm, v(4.9, 32.88) * mm]});
            skFitSpline(sketch, "E286", {"points": [v(4.9, 32.88) * mm, v(3.5, 33.5) * mm, v(2.36, 34.42) * mm, v(1.34, 35.53) * mm]});
            skFitSpline(sketch, "E287", {"points": [v(1.34, 35.53) * mm, v(0.04, 36.96) * mm, v(-0.59, 38.66) * mm, v(-0.74, 40.57) * mm]});
            skFitSpline(sketch, "E288", {"points": [v(-0.74, 40.57) * mm, v(-0.8, 41.38) * mm, v(-1, 42.17) * mm, v(-0.94, 43) * mm]});
            skFitSpline(sketch, "E289", {"points": [v(-0.94, 43) * mm, v(-0.85, 44.55) * mm, v(0.53, 45.67) * mm, v(2.04, 45.42) * mm]});
            skFitSpline(sketch, "E290", {"points": [v(2.04, 45.42) * mm, v(3.57, 45.16) * mm, v(5.04, 44.69) * mm, v(6.55, 44.35) * mm]});
            skFitSpline(sketch, "E291", {"points": [v(6.55, 44.35) * mm, v(8.37, 43.95) * mm, v(10.2, 43.7) * mm, v(12.06, 43.72) * mm]});
            skFitSpline(sketch, "E292", {"points": [v(12.06, 43.72) * mm, v(14.87, 43.77) * mm, v(17.47, 42.99) * mm, v(20.03, 41.9) * mm]});
            skFitSpline(sketch, "E293", {"points": [v(20.03, 41.9) * mm, v(22.15, 41) * mm, v(24.19, 39.94) * mm, v(26.08, 38.6) * mm]});
            skFitSpline(sketch, "E294", {"points": [v(26.08, 38.6) * mm, v(26.17, 38.53) * mm, v(26.25, 38.43) * mm, v(26.44, 38.49) * mm]});
            skFitSpline(sketch, "E295", {"points": [v(26.44, 38.49) * mm, v(25.56, 39.48) * mm, v(24.9, 40.61) * mm, v(24.5, 41.84) * mm]});
            skFitSpline(sketch, "E296", {"points": [v(24.5, 41.84) * mm, v(23.83, 43.93) * mm, v(23.78, 46.02) * mm, v(25.03, 47.97) * mm]});
            skFitSpline(sketch, "E297", {"points": [v(25.03, 47.97) * mm, v(25.46, 48.64) * mm, v(26.12, 49) * mm, v(26.82, 49.4) * mm]});
            skFitSpline(sketch, "E298", {"points": [v(26.82, 49.4) * mm, v(25.63, 50.1) * mm, v(24.78, 51.15) * mm, v(23.76, 52) * mm]});
            skFitSpline(sketch, "E299", {"points": [v(23.76, 52) * mm, v(22.25, 53.27) * mm, v(20.44, 53.7) * mm, v(18.55, 53.75) * mm]});
            skFitSpline(sketch, "E300", {"points": [v(18.55, 53.75) * mm, v(17.1, 53.78) * mm, v(15.64, 53.72) * mm, v(14.19, 53.67) * mm]});
            skFitSpline(sketch, "E301", {"points": [v(14.19, 53.67) * mm, v(9.06, 53.52) * mm, v(4.2, 54.58) * mm, v(-0.26, 57.24) * mm]});
            skFitSpline(sketch, "E302", {"points": [v(-0.26, 57.24) * mm, v(-2.15, 58.37) * mm, v(-4.03, 59.52) * mm, v(-6.07, 60.37) * mm]});
            skFitSpline(sketch, "E303", {"points": [v(-6.07, 60.37) * mm, v(-8.01, 61.18) * mm, v(-10.04, 61.62) * mm, v(-12.13, 61.77) * mm]});
            skFitSpline(sketch, "E304", {"points": [v(-12.13, 61.77) * mm, v(-12.45, 61.8) * mm, v(-12.78, 61.8) * mm, v(-13.07, 61.96) * mm]});
            skFitSpline(sketch, "E305", {"points": [v(-13.17, 61.96) * mm, v(-13.5, 61.88) * mm, v(-13.84, 61.88) * mm, v(-14.17, 61.96) * mm]});
            skFitSpline(sketch, "E306", {"points": [v(-42.85, 34.16) * mm, v(-42.6, 33.55) * mm, v(-42.66, 32.89) * mm, v(-42.57, 32.25) * mm]});
            skFitSpline(sketch, "E307", {"points": [v(-42.57, 32.25) * mm, v(-41.63, 25.4) * mm, v(-38.8, 19.57) * mm, v(-33.58, 15.04) * mm]});
            skFitSpline(sketch, "E308", {"points": [v(-33.58, 15.04) * mm, v(-30.64, 12.5) * mm, v(-27.24, 10.89) * mm, v(-23.4, 10.27) * mm]});
            skFitSpline(sketch, "E309", {"points": [v(-23.4, 10.27) * mm, v(-21.75, 10) * mm, v(-20.07, 10.08) * mm, v(-18.4, 10.01) * mm]});
            skFitSpline(sketch, "E310", {"points": [v(-18.4, 10.01) * mm, v(-17.32, 9.97) * mm, v(-16.24, 9.98) * mm, v(-15.16, 9.75) * mm]});
            skFitSpline(sketch, "E311", {"points": [v(-15.16, 9.75) * mm, v(-13.94, 9.5) * mm, v(-13.02, 8.84) * mm, v(-12.34, 7.82) * mm]});
            skFitSpline(sketch, "E312", {"points": [v(-12.34, 7.82) * mm, v(-12.12, 7.48) * mm, v(-11.9, 7.13) * mm, v(-11.74, 6.76) * mm]});
            skFitSpline(sketch, "E313", {"points": [v(-11.74, 6.76) * mm, v(-10.3, 3.3) * mm, v(-8.86, -0.17) * mm, v(-8.04, -3.86) * mm]});
            skFitSpline(sketch, "E314", {"points": [v(-8.04, -3.86) * mm, v(-7.85, -4.74) * mm, v(-7.75, -5.63) * mm, v(-7.8, -6.53) * mm]});
            skFitSpline(sketch, "E315", {"points": [v(-7.8, -6.53) * mm, v(-7.87, -7.98) * mm, v(-8.87, -8.66) * mm, v(-10.2, -8.17) * mm]});
            skFitSpline(sketch, "E316", {"points": [v(-10.2, -8.17) * mm, v(-10.5, -8.06) * mm, v(-10.77, -7.92) * mm, v(-11.11, -7.77) * mm]});
            skFitSpline(sketch, "E317", {"points": [v(-11.11, -7.77) * mm, v(-10.83, -8.76) * mm, v(-10.4, -9.55) * mm, v(-9.6, -10.14) * mm]});
            skFitSpline(sketch, "E318", {"points": [v(-9.6, -10.14) * mm, v(-8.24, -11.18) * mm, v(-6.68, -11.65) * mm, v(-5.02, -11.86) * mm]});
            skFitSpline(sketch, "E319", {"points": [v(-5.02, -11.86) * mm, v(-3.36, -12.08) * mm, v(-1.69, -12.11) * mm, v(-0.02, -12.17) * mm]});
            skFitSpline(sketch, "E320", {"points": [v(-0.02, -12.17) * mm, v(1.77, -12.22) * mm, v(3.54, -12.5) * mm, v(5.32, -12.72) * mm]});
            skFitSpline(sketch, "E321", {"points": [v(5.32, -12.72) * mm, v(8.35, -13.1) * mm, v(11.34, -13.75) * mm, v(14.36, -14.21) * mm]});
            skFitSpline(sketch, "E322", {"points": [v(14.36, -14.21) * mm, v(15.18, -14.34) * mm, v(15.97, -14.63) * mm, v(16.8, -14.73) * mm]});
            skFitSpline(sketch, "E323", {"points": [v(16.8, -14.73) * mm, v(16.9, -14.75) * mm, v(17.02, -14.82) * mm, v(17.01, -14.63) * mm]});
            skFitSpline(sketch, "E324", {"points": [v(17.01, -14.63) * mm, v(12.02, -12.4) * mm, v(7.75, -9.18) * mm, v(4.03, -5.13) * mm]});
            skFitSpline(sketch, "E325", {"points": [v(4.03, -5.13) * mm, v(2.16, -3.09) * mm, v(0.67, -0.8) * mm, v(-0.78, 1.53) * mm]});
            skFitSpline(sketch, "E326", {"points": [v(-0.78, 1.53) * mm, v(-4.46, 7.42) * mm, v(-6.77, 13.86) * mm, v(-8.17, 20.65) * mm]});
            skFitSpline(sketch, "E327", {"points": [v(-8.17, 20.65) * mm, v(-8.35, 21.53) * mm, v(-8.42, 22.43) * mm, v(-8.82, 23.24) * mm]});
            skFitSpline(sketch, "E328", {"points": [v(-8.82, 23.24) * mm, v(-9.7, 25.03) * mm, v(-11.2, 25.93) * mm, v(-13, 26.38) * mm]});
            skFitSpline(sketch, "E329", {"points": [v(-13, 26.38) * mm, v(-13.23, 26.44) * mm, v(-13.46, 26.48) * mm, v(-13.7, 26.5) * mm]});
            skFitSpline(sketch, "E330", {"points": [v(-13.7, 26.5) * mm, v(-14.73, 26.63) * mm, v(-15.75, 26.77) * mm, v(-16.72, 27.26) * mm]});
            skFitSpline(sketch, "E331", {"points": [v(-16.72, 27.26) * mm, v(-16.76, 26.85) * mm, v(-16.57, 26.54) * mm, v(-16.48, 26.2) * mm]});
            skFitSpline(sketch, "E332", {"points": [v(-16.48, 26.2) * mm, v(-16, 24.4) * mm, v(-15.74, 22.58) * mm, v(-16, 20.73) * mm]});
            skFitSpline(sketch, "E333", {"points": [v(-16, 20.73) * mm, v(-16.34, 18.26) * mm, v(-17.79, 16.82) * mm, v(-20.15, 16.25) * mm]});
            skFitSpline(sketch, "E334", {"points": [v(-20.15, 16.25) * mm, v(-23.4, 15.45) * mm, v(-26.44, 16.11) * mm, v(-29.3, 17.73) * mm]});
            skFitSpline(sketch, "E335", {"points": [v(-29.3, 17.73) * mm, v(-32.8, 19.7) * mm, v(-35.18, 22.74) * mm, v(-36.93, 26.32) * mm]});
            skFitSpline(sketch, "E336", {"points": [v(-36.93, 26.32) * mm, v(-38.65, 29.84) * mm, v(-39.63, 33.57) * mm, v(-39.2, 37.5) * mm]});
            skFitSpline(sketch, "E337", {"points": [v(-39.2, 37.5) * mm, v(-38.63, 42.7) * mm, v(-36.87, 47.38) * mm, v(-32.6, 50.7) * mm]});
            skFitSpline(sketch, "E338", {"points": [v(-32.6, 50.7) * mm, v(-31, 51.94) * mm, v(-29.21, 52.95) * mm, v(-27.17, 53.25) * mm]});
            skFitSpline(sketch, "E339", {"points": [v(-27.17, 53.25) * mm, v(-24.16, 53.7) * mm, v(-21.31, 53.26) * mm, v(-18.96, 51.14) * mm]});
            skFitSpline(sketch, "E340", {"points": [v(-18.96, 51.14) * mm, v(-17.44, 49.76) * mm, v(-17.08, 47.92) * mm, v(-17.36, 45.94) * mm]});
            skFitSpline(sketch, "E341", {"points": [v(-17.36, 45.94) * mm, v(-17.41, 45.6) * mm, v(-17.63, 45.32) * mm, v(-17.87, 45.07) * mm]});
            skFitSpline(sketch, "E342", {"points": [v(-17.87, 45.07) * mm, v(-18.18, 44.74) * mm, v(-18.5, 44.41) * mm, v(-18.82, 44.07) * mm]});
            skFitSpline(sketch, "E343", {"points": [v(-18.82, 44.07) * mm, v(-17.8, 43.58) * mm, v(-17.01, 42.78) * mm, v(-16.24, 41.96) * mm]});
            skFitSpline(sketch, "E344", {"points": [v(-16.24, 41.96) * mm, v(-15.3, 40.97) * mm, v(-14.34, 40.01) * mm, v(-13.2, 39.25) * mm]});
            skFitSpline(sketch, "E345", {"points": [v(-13.2, 39.25) * mm, v(-12.69, 38.9) * mm, v(-12.15, 38.94) * mm, v(-11.61, 38.96) * mm]});
            skFitSpline(sketch, "E346", {"points": [v(-11.61, 38.96) * mm, v(-11.36, 38.97) * mm, v(-11.24, 39.24) * mm, v(-11.12, 39.43) * mm]});
            skFitSpline(sketch, "E347", {"points": [v(-11.12, 39.43) * mm, v(-10.82, 39.9) * mm, v(-10.67, 40.43) * mm, v(-10.62, 40.96) * mm]});
            skFitSpline(sketch, "E348", {"points": [v(-10.62, 40.96) * mm, v(-10.29, 44.25) * mm, v(-10.66, 47.45) * mm, v(-11.87, 50.53) * mm]});
            skFitSpline(sketch, "E349", {"points": [v(-11.87, 50.53) * mm, v(-12.63, 52.45) * mm, v(-13.6, 54.26) * mm, v(-15, 55.8) * mm]});
            skFitSpline(sketch, "E350", {"points": [v(-15, 55.8) * mm, v(-16.53, 57.5) * mm, v(-18.38, 58.65) * mm, v(-20.61, 59.1) * mm]});
            skFitSpline(sketch, "E351", {"points": [v(-20.61, 59.1) * mm, v(-26.57, 60.31) * mm, v(-31.67, 58.5) * mm, v(-36.12, 54.5) * mm]});
            skFitSpline(sketch, "E352", {"points": [v(-36.12, 54.5) * mm, v(-38.56, 52.3) * mm, v(-39.83, 49.38) * mm, v(-40.94, 46.37) * mm]});
            skFitSpline(sketch, "E353", {"points": [v(-40.94, 46.37) * mm, v(-41.85, 43.9) * mm, v(-42.33, 41.33) * mm, v(-42.66, 38.73) * mm]});
            skFitSpline(sketch, "E354", {"points": [v(-42.66, 38.73) * mm, v(-42.7, 38.46) * mm, v(-42.67, 38.17) * mm, v(-42.85, 37.93) * mm]});
            skFitSpline(sketch, "E355", {"points": [v(-42.85, 36.81) * mm, v(-42.77, 36.37) * mm, v(-42.77, 35.93) * mm, v(-42.85, 35.49) * mm]});
            skFitSpline(sketch, "E356", {"points": [v(-42.85, 34.98) * mm, v(-42.8, 34.91) * mm, v(-42.8, 34.84) * mm, v(-42.85, 34.78) * mm]});
            skFitSpline(sketch, "E357", {"points": [v(40.63, -16.62) * mm, v(40.03, -16.65) * mm, v(39.42, -16.48) * mm, v(38.83, -16.7) * mm]});
            skFitSpline(sketch, "E358", {"points": [v(-42.85, 35.49) * mm, v(-42.69, 35.93) * mm, v(-42.69, 36.37) * mm, v(-42.85, 36.81) * mm]});
            skFitSpline(sketch, "E359", {"points": [v(-14.22, 61.96) * mm, v(-13.88, 61.8) * mm, v(-13.55, 61.8) * mm, v(-13.21, 61.96) * mm]});
            skFitSpline(sketch, "E360", {"points": [v(-42.85, 34.77) * mm, v(-42.7, 34.84) * mm, v(-42.72, 34.91) * mm, v(-42.85, 34.98) * mm]});
            skFitSpline(sketch, "E361", {"points": [v(36.2, -31.09) * mm, v(36.2, -31.19) * mm, v(36.14, -31.33) * mm, v(36.03, -31.52) * mm]});
            skFitSpline(sketch, "E362", {"points": [v(35.01, -30.98) * mm, v(34.51, -30.8) * mm, v(33.97, -30.7) * mm, v(33.37, -30.7) * mm]});
            skFitSpline(sketch, "E363", {"points": [v(27.52, -30.26) * mm, v(27.27, -29.84) * mm, v(27.06, -29.54) * mm, v(26.88, -29.35) * mm]});
            skFitSpline(sketch, "E364", {"points": [v(26.9, -29.28) * mm, v(26.91, -29.26) * mm, v(26.95, -29.22) * mm, v(27.02, -29.17) * mm]});
            skFitSpline(sketch, "E365", {"points": [v(27.02, -29.17) * mm, v(27.1, -29.12) * mm, v(27.16, -29.1) * mm, v(27.2, -29.1) * mm]});
            skFitSpline(sketch, "E366", {"points": [v(27.2, -29.1) * mm, v(27.32, -29.1) * mm, v(27.44, -29.17) * mm, v(27.55, -29.3) * mm]});
            skFitSpline(sketch, "E367", {"points": [v(27.55, -29.3) * mm, v(27.67, -29.44) * mm, v(27.78, -29.53) * mm, v(27.9, -29.57) * mm]});
            skFitSpline(sketch, "E368", {"points": [v(27.9, -29.57) * mm, v(28.63, -29.7) * mm, v(29.44, -29.76) * mm, v(30.32, -29.76) * mm]});
            skFitSpline(sketch, "E369", {"points": [v(34.41, -29.76) * mm, v(34.56, -29.76) * mm, v(34.8, -29.83) * mm, v(35.12, -29.97) * mm]});
            skFitSpline(sketch, "E370", {"points": [v(35.12, -29.97) * mm, v(35.46, -30.15) * mm, v(35.73, -30.31) * mm, v(35.93, -30.47) * mm]});
            skFitSpline(sketch, "E371", {"points": [v(35.93, -30.47) * mm, v(36.1, -30.6) * mm, v(36.2, -30.81) * mm, v(36.2, -31.09) * mm]});
            skFitSpline(sketch, "E372", {"points": [v(37.7, -29.32) * mm, v(38.17, -28.53) * mm, v(38.41, -27.65) * mm, v(38.41, -26.7) * mm]});
            skFitSpline(sketch, "E373", {"points": [v(38.41, -26.7) * mm, v(38.41, -26.04) * mm, v(38.22, -25.5) * mm, v(37.83, -25.09) * mm]});
            skFitSpline(sketch, "E374", {"points": [v(37.83, -25.09) * mm, v(37.44, -24.67) * mm, v(36.94, -24.4) * mm, v(36.33, -24.26) * mm]});
            skFitSpline(sketch, "E375", {"points": [v(36.33, -24.26) * mm, v(35.71, -24.13) * mm, v(34.95, -24.06) * mm, v(34.05, -24.06) * mm]});
            skFitSpline(sketch, "E376", {"points": [v(29.36, -24.3) * mm, v(28.94, -24.3) * mm, v(28.54, -24.31) * mm, v(28.15, -24.33) * mm]});
            skFitSpline(sketch, "E377", {"points": [v(28.15, -24.33) * mm, v(27.77, -24.35) * mm, v(27.48, -24.37) * mm, v(27.3, -24.39) * mm]});
            skFitSpline(sketch, "E378", {"points": [v(27.09, -23.13) * mm, v(28, -23.03) * mm, v(28.78, -22.97) * mm, v(29.45, -22.97) * mm]});
            skFitSpline(sketch, "E379", {"points": [v(36.14, -22.66) * mm, v(37.23, -22.66) * mm, v(38, -22.85) * mm, v(38.45, -23.23) * mm]});
            skFitSpline(sketch, "E380", {"points": [v(38.45, -23.23) * mm, v(38.93, -23.57) * mm, v(39.17, -24.28) * mm, v(39.17, -25.34) * mm]});
            skFitSpline(sketch, "E381", {"points": [v(39.17, -25.34) * mm, v(39.17, -26.27) * mm, v(39.07, -27.09) * mm, v(38.87, -27.8) * mm]});
            skFitSpline(sketch, "E382", {"points": [v(38.87, -27.8) * mm, v(38.67, -28.5) * mm, v(38.4, -29.07) * mm, v(38.04, -29.5) * mm]});
            skFitSpline(sketch, "E383", {"points": [v(41.6, -35.22) * mm, v(41.97, -35.64) * mm, v(42.27, -36.2) * mm, v(42.5, -36.9) * mm]});
            skFitSpline(sketch, "E384", {"points": [v(42.5, -36.9) * mm, v(42.74, -37.59) * mm, v(42.85, -38.1) * mm, v(42.85, -38.46) * mm]});
            skFitSpline(sketch, "E385", {"points": [v(42.85, -38.46) * mm, v(42.85, -39.3) * mm, v(42.5, -39.99) * mm, v(41.78, -40.53) * mm]});
            skFitSpline(sketch, "E386", {"points": [v(41.78, -40.53) * mm, v(41.06, -41.07) * mm, v(40, -41.34) * mm, v(38.6, -41.34) * mm]});
            skFitSpline(sketch, "E387", {"points": [v(38.6, -41.34) * mm, v(38.15, -41.34) * mm, v(37.7, -41.28) * mm, v(37.25, -41.15) * mm]});
            skFitSpline(sketch, "E388", {"points": [v(37.25, -41.15) * mm, v(36.8, -41.02) * mm, v(36.23, -40.79) * mm, v(35.56, -40.46) * mm]});
            skFitSpline(sketch, "E389", {"points": [v(35.56, -40.46) * mm, v(34.89, -40.13) * mm, v(34.18, -39.58) * mm, v(33.43, -38.82) * mm]});
            skFitSpline(sketch, "E390", {"points": [v(33.43, -38.82) * mm, v(32.68, -38.05) * mm, v(32.09, -37.3) * mm, v(31.65, -36.54) * mm]});
            skFitSpline(sketch, "E391", {"points": [v(31.65, -36.54) * mm, v(31.22, -35.8) * mm, v(30.9, -34.88) * mm, v(30.71, -33.8) * mm]});
            skFitSpline(sketch, "E392", {"points": [v(30.71, -33.8) * mm, v(30.52, -32.72) * mm, v(30.36, -31.52) * mm, v(30.25, -30.2) * mm]});
            skFitSpline(sketch, "E393", {"points": [v(29.88, -26.54) * mm, v(29.74, -25.38) * mm, v(29.63, -24.72) * mm, v(29.55, -24.56) * mm]});
            skFitSpline(sketch, "E394", {"points": [v(29.3, -24.3) * mm, v(29.2, -24.2) * mm, v(29.15, -24.15) * mm, v(29.13, -24.1) * mm]});
            skFitSpline(sketch, "E395", {"points": [v(29.13, -24.1) * mm, v(29.11, -24.07) * mm, v(29.1, -24.04) * mm, v(29.08, -24) * mm]});
            skFitSpline(sketch, "E396", {"points": [v(29.08, -24) * mm, v(29.12, -23.98) * mm, v(29.15, -23.96) * mm, v(29.18, -23.96) * mm]});
            skFitSpline(sketch, "E397", {"points": [v(29.55, -24.04) * mm, v(30.22, -24.23) * mm, v(30.7, -24.7) * mm, v(31.01, -25.46) * mm]});
            skFitSpline(sketch, "E398", {"points": [v(31.01, -25.46) * mm, v(31.32, -26.2) * mm, v(31.52, -26.85) * mm, v(31.61, -27.39) * mm]});
            skFitSpline(sketch, "E399", {"points": [v(31.61, -27.39) * mm, v(31.71, -27.92) * mm, v(31.76, -28.48) * mm, v(31.76, -29.06) * mm]});
            skFitSpline(sketch, "E400", {"points": [v(31.88, -31.82) * mm, v(31.88, -32.1) * mm, v(31.89, -32.36) * mm, v(31.92, -32.58) * mm]});
            skFitSpline(sketch, "E401", {"points": [v(31.92, -32.58) * mm, v(31.94, -32.8) * mm, v(32, -33.16) * mm, v(32.07, -33.64) * mm]});
            skFitSpline(sketch, "E402", {"points": [v(32.07, -33.64) * mm, v(32.15, -34.3) * mm, v(32.27, -34.99) * mm, v(32.45, -35.7) * mm]});
            skFitSpline(sketch, "E403", {"points": [v(32.45, -35.7) * mm, v(32.62, -36.42) * mm, v(32.86, -37.03) * mm, v(33.17, -37.52) * mm]});
            skFitSpline(sketch, "E404", {"points": [v(33.17, -37.52) * mm, v(33.47, -38.01) * mm, v(33.84, -38.43) * mm, v(34.26, -38.78) * mm]});
            skFitSpline(sketch, "E405", {"points": [v(34.26, -38.78) * mm, v(34.69, -39.09) * mm, v(35.16, -39.32) * mm, v(35.68, -39.48) * mm]});
            skFitSpline(sketch, "E406", {"points": [v(35.68, -39.48) * mm, v(36.2, -39.63) * mm, v(36.72, -39.71) * mm, v(37.27, -39.71) * mm]});
            skFitSpline(sketch, "E407", {"points": [v(38.3, -39.63) * mm, v(38.88, -39.54) * mm, v(39.37, -39.44) * mm, v(39.78, -39.32) * mm]});
            skFitSpline(sketch, "E408", {"points": [v(39.78, -39.32) * mm, v(40.19, -39.2) * mm, v(40.56, -39.06) * mm, v(40.88, -38.89) * mm]});
            skFitSpline(sketch, "E409", {"points": [v(40.88, -38.89) * mm, v(41.21, -38.72) * mm, v(41.47, -38.5) * mm, v(41.65, -38.22) * mm]});
            skFitSpline(sketch, "E410", {"points": [v(41.65, -38.22) * mm, v(41.83, -37.95) * mm, v(41.92, -37.64) * mm, v(41.92, -37.28) * mm]});
            skFitSpline(sketch, "E411", {"points": [v(41.92, -37.28) * mm, v(41.92, -37.03) * mm, v(41.88, -36.79) * mm, v(41.8, -36.55) * mm]});
            skFitSpline(sketch, "E412", {"points": [v(41.8, -36.55) * mm, v(41.73, -36.31) * mm, v(41.63, -36.11) * mm, v(41.52, -35.94) * mm]});
            skFitSpline(sketch, "E413", {"points": [v(41.52, -35.94) * mm, v(41.46, -35.83) * mm, v(41.42, -35.74) * mm, v(41.37, -35.68) * mm]});
            skFitSpline(sketch, "E414", {"points": [v(41.37, -35.68) * mm, v(41.32, -35.62) * mm, v(41.25, -35.53) * mm, v(41.15, -35.4) * mm]});
            skFitSpline(sketch, "E415", {"points": [v(40.72, -34.76) * mm, v(40.72, -34.65) * mm, v(40.78, -34.6) * mm, v(40.91, -34.6) * mm]});
            skFitSpline(sketch, "E416", {"points": [v(40.91, -34.6) * mm, v(41, -34.6) * mm, v(41.23, -34.8) * mm, v(41.6, -35.22) * mm]});
            skFitSpline(sketch, "E417", {"points": [v(24.15, -33.75) * mm, v(24.06, -33.18) * mm, v(23.87, -31.77) * mm, v(23.56, -29.53) * mm]});
            skFitSpline(sketch, "E418", {"points": [v(23.5, -28.89) * mm, v(23.5, -28.54) * mm, v(23.58, -28.37) * mm, v(23.75, -28.37) * mm]});
            skFitSpline(sketch, "E419", {"points": [v(23.75, -28.37) * mm, v(23.88, -28.37) * mm, v(24.04, -28.42) * mm, v(24.23, -28.54) * mm]});
            skFitSpline(sketch, "E420", {"points": [v(26.33, -30.01) * mm, v(26.43, -30.09) * mm, v(26.48, -30.19) * mm, v(26.48, -30.3) * mm]});
            skFitSpline(sketch, "E421", {"points": [v(26.17, -30.3) * mm, v(26.07, -30.28) * mm, v(25.91, -30.2) * mm, v(25.7, -30.04) * mm]});
            skFitSpline(sketch, "E422", {"points": [v(25.7, -30.04) * mm, v(25.49, -29.9) * mm, v(25.34, -29.82) * mm, v(25.26, -29.82) * mm]});
            skFitSpline(sketch, "E423", {"points": [v(25.26, -29.82) * mm, v(25.19, -29.82) * mm, v(25.15, -29.98) * mm, v(25.15, -30.3) * mm]});
            skFitSpline(sketch, "E424", {"points": [v(25.79, -35.64) * mm, v(25.8, -35.72) * mm, v(25.82, -35.8) * mm, v(25.83, -35.86) * mm]});
            skFitSpline(sketch, "E425", {"points": [v(25.83, -35.86) * mm, v(25.85, -35.93) * mm, v(25.87, -35.98) * mm, v(25.88, -36) * mm]});
            skFitSpline(sketch, "E426", {"points": [v(24.4, -35.44) * mm, v(24.32, -34.88) * mm, v(24.23, -34.32) * mm, v(24.15, -33.75) * mm]});
            skFitSpline(sketch, "E427", {"points": [v(21.46, -30.67) * mm, v(20.87, -29.75) * mm, v(20.57, -29.17) * mm, v(20.57, -28.93) * mm]});
            skFitSpline(sketch, "E428", {"points": [v(20.57, -28.93) * mm, v(20.57, -28.55) * mm, v(20.73, -28.37) * mm, v(21.05, -28.37) * mm]});
            skFitSpline(sketch, "E429", {"points": [v(21.05, -28.37) * mm, v(21.3, -28.37) * mm, v(21.63, -28.5) * mm, v(22.03, -28.76) * mm]});
            skFitSpline(sketch, "E430", {"points": [v(22.03, -28.76) * mm, v(22.44, -29.03) * mm, v(22.83, -29.4) * mm, v(23.19, -29.85) * mm]});
            skFitSpline(sketch, "E431", {"points": [v(23.89, -30.75) * mm, v(24.12, -30.85) * mm, v(24.23, -31.02) * mm, v(24.23, -31.25) * mm]});
            skFitSpline(sketch, "E432", {"points": [v(24.23, -31.25) * mm, v(24.23, -31.3) * mm, v(24.2, -31.35) * mm, v(24.14, -31.4) * mm]});
            skFitSpline(sketch, "E433", {"points": [v(24.14, -31.4) * mm, v(24.03, -31.4) * mm, v(23.87, -31.33) * mm, v(23.65, -31.18) * mm]});
            skFitSpline(sketch, "E434", {"points": [v(23.19, -30.77) * mm, v(22.74, -30.3) * mm, v(22.42, -30.07) * mm, v(22.24, -30.07) * mm]});
            skFitSpline(sketch, "E435", {"points": [v(22.24, -30.07) * mm, v(22.15, -30.07) * mm, v(22.1, -30.14) * mm, v(22.1, -30.27) * mm]});
            skFitSpline(sketch, "E436", {"points": [v(22.1, -30.27) * mm, v(22.1, -30.43) * mm, v(22.16, -30.68) * mm, v(22.27, -31) * mm]});
            skFitSpline(sketch, "E437", {"points": [v(22.27, -31) * mm, v(22.38, -31.33) * mm, v(22.44, -31.56) * mm, v(22.47, -31.7) * mm]});
            skFitSpline(sketch, "E438", {"points": [v(22.47, -31.7) * mm, v(22.5, -31.84) * mm, v(22.52, -31.96) * mm, v(22.53, -32.05) * mm]});
            skFitSpline(sketch, "E439", {"points": [v(22.53, -32.05) * mm, v(22.41, -32.05) * mm, v(22.06, -31.59) * mm, v(21.46, -30.67) * mm]});
            skFitSpline(sketch, "E440", {"points": [v(15.02, -29.33) * mm, v(14.92, -29.28) * mm, v(14.83, -29.19) * mm, v(14.76, -29.06) * mm]});
            skFitSpline(sketch, "E441", {"points": [v(14.76, -29.06) * mm, v(14.7, -28.94) * mm, v(14.65, -28.82) * mm, v(14.65, -28.72) * mm]});
            skFitSpline(sketch, "E442", {"points": [v(14.65, -28.72) * mm, v(14.65, -28.52) * mm, v(14.85, -28.42) * mm, v(15.24, -28.42) * mm]});
            skFitSpline(sketch, "E443", {"points": [v(16.71, -28.55) * mm, v(17.06, -28.55) * mm, v(17.39, -28.64) * mm, v(17.7, -28.8) * mm]});
            skFitSpline(sketch, "E444", {"points": [v(17.7, -28.8) * mm, v(18, -28.96) * mm, v(18.35, -29.24) * mm, v(18.73, -29.65) * mm]});
            skFitSpline(sketch, "E445", {"points": [v(18.73, -29.65) * mm, v(19.1, -30.06) * mm, v(19.4, -30.54) * mm, v(19.6, -31.09) * mm]});
            skFitSpline(sketch, "E446", {"points": [v(19.6, -31.09) * mm, v(19.8, -31.63) * mm, v(19.96, -32.08) * mm, v(20.05, -32.43) * mm]});
            skFitSpline(sketch, "E447", {"points": [v(20.05, -32.43) * mm, v(20.14, -32.78) * mm, v(20.2, -33.1) * mm, v(20.25, -33.38) * mm]});
            skFitSpline(sketch, "E448", {"points": [v(20.25, -33.38) * mm, v(20.3, -33.67) * mm, v(20.32, -33.9) * mm, v(20.34, -34.1) * mm]});
            skFitSpline(sketch, "E449", {"points": [v(20.34, -34.1) * mm, v(20.35, -34.28) * mm, v(20.36, -34.42) * mm, v(20.36, -34.5) * mm]});
            skFitSpline(sketch, "E450", {"points": [v(20.36, -34.5) * mm, v(20.36, -35.53) * mm, v(20.07, -36.04) * mm, v(19.5, -36.04) * mm]});
            skFitSpline(sketch, "E451", {"points": [v(19.5, -36.04) * mm, v(18.97, -36.04) * mm, v(18.24, -35.55) * mm, v(17.3, -34.56) * mm]});
            skFitSpline(sketch, "E452", {"points": [v(16.63, -33.84) * mm, v(16.43, -33.63) * mm, v(16.26, -33.42) * mm, v(16.13, -33.2) * mm]});
            skFitSpline(sketch, "E453", {"points": [v(16.13, -33.2) * mm, v(16, -32.97) * mm, v(15.93, -32.75) * mm, v(15.93, -32.53) * mm]});
            skFitSpline(sketch, "E454", {"points": [v(15.93, -32.53) * mm, v(15.93, -32.47) * mm, v(15.96, -32.39) * mm, v(16.01, -32.3) * mm]});
            skFitSpline(sketch, "E455", {"points": [v(16.46, -32.84) * mm, v(16.73, -33.22) * mm, v(17.05, -33.61) * mm, v(17.43, -34) * mm]});
            skFitSpline(sketch, "E456", {"points": [v(17.43, -34) * mm, v(17.8, -34.4) * mm, v(18.13, -34.6) * mm, v(18.4, -34.6) * mm]});
            skFitSpline(sketch, "E457", {"points": [v(18.4, -34.6) * mm, v(18.72, -34.6) * mm, v(18.88, -34.26) * mm, v(18.88, -33.58) * mm]});
            skFitSpline(sketch, "E458", {"points": [v(18.88, -33.58) * mm, v(18.88, -33.1) * mm, v(18.81, -32.5) * mm, v(18.68, -31.8) * mm]});
            skFitSpline(sketch, "E459", {"points": [v(18.68, -31.8) * mm, v(18.54, -31.1) * mm, v(18.39, -30.58) * mm, v(18.21, -30.24) * mm]});
            skFitSpline(sketch, "E460", {"points": [v(18.21, -30.24) * mm, v(18.04, -29.9) * mm, v(17.85, -29.68) * mm, v(17.65, -29.57) * mm]});
            skFitSpline(sketch, "E461", {"points": [v(17.65, -29.57) * mm, v(17.45, -29.46) * mm, v(17.22, -29.4) * mm, v(16.96, -29.4) * mm]});
            skFitSpline(sketch, "E462", {"points": [v(14.54, -29.14) * mm, v(14.54, -28.69) * mm, v(14.68, -28.46) * mm, v(14.97, -28.46) * mm]});
            skFitSpline(sketch, "E463", {"points": [v(14.97, -28.46) * mm, v(15.12, -28.46) * mm, v(15.3, -28.55) * mm, v(15.53, -28.73) * mm]});
            skFitSpline(sketch, "E464", {"points": [v(15.53, -28.73) * mm, v(15.72, -28.93) * mm, v(15.88, -29.18) * mm, v(16, -29.48) * mm]});
            skFitSpline(sketch, "E465", {"points": [v(16, -29.48) * mm, v(16.12, -29.78) * mm, v(16.2, -30.05) * mm, v(16.26, -30.28) * mm]});
            skFitSpline(sketch, "E466", {"points": [v(16.26, -30.28) * mm, v(16.31, -30.5) * mm, v(16.35, -30.78) * mm, v(16.38, -31.1) * mm]});
            skFitSpline(sketch, "E467", {"points": [v(16.85, -35.3) * mm, v(16.85, -35.79) * mm, v(16.74, -36.03) * mm, v(16.52, -36.03) * mm]});
            skFitSpline(sketch, "E468", {"points": [v(16.52, -36.03) * mm, v(16.3, -36.03) * mm, v(16.02, -35.88) * mm, v(15.66, -35.6) * mm]});
            skFitSpline(sketch, "E469", {"points": [v(15.66, -35.6) * mm, v(15.3, -35.35) * mm, v(14.71, -34.87) * mm, v(13.9, -34.14) * mm]});
            skFitSpline(sketch, "E470", {"points": [v(13.9, -34.14) * mm, v(13.85, -34.08) * mm, v(13.8, -34.03) * mm, v(13.78, -33.99) * mm]});
            skFitSpline(sketch, "E471", {"points": [v(13.78, -33.99) * mm, v(13.76, -33.95) * mm, v(13.74, -33.91) * mm, v(13.72, -33.87) * mm]});
            skFitSpline(sketch, "E472", {"points": [v(13.72, -33.87) * mm, v(13.72, -33.85) * mm, v(13.76, -33.81) * mm, v(13.82, -33.78) * mm]});
            skFitSpline(sketch, "E473", {"points": [v(13.82, -33.78) * mm, v(13.91, -33.78) * mm, v(14.02, -33.82) * mm, v(14.16, -33.91) * mm]});
            skFitSpline(sketch, "E474", {"points": [v(14.16, -33.91) * mm, v(14.3, -34) * mm, v(14.42, -34.1) * mm, v(14.54, -34.18) * mm]});
            skFitSpline(sketch, "E475", {"points": [v(14.54, -34.18) * mm, v(14.65, -34.27) * mm, v(14.76, -34.36) * mm, v(14.85, -34.45) * mm]});
            skFitSpline(sketch, "E476", {"points": [v(15.26, -34.75) * mm, v(15.27, -34.73) * mm, v(15.28, -34.71) * mm, v(15.3, -34.68) * mm]});
            skFitSpline(sketch, "E477", {"points": [v(15.3, -34.68) * mm, v(15.32, -34.65) * mm, v(15.33, -34.6) * mm, v(15.33, -34.51) * mm]});
            skFitSpline(sketch, "E478", {"points": [v(8.27, -29.31) * mm, v(8.17, -29.25) * mm, v(8.1, -29.17) * mm, v(8.04, -29.08) * mm]});
            skFitSpline(sketch, "E479", {"points": [v(7.89, -28.74) * mm, v(7.89, -28.55) * mm, v(8.08, -28.46) * mm, v(8.47, -28.35) * mm]});
            skFitSpline(sketch, "E480", {"points": [v(10.14, -28.6) * mm, v(10.8, -28.66) * mm, v(11.4, -28.9) * mm, v(11.9, -29.32) * mm]});
            skFitSpline(sketch, "E481", {"points": [v(11.9, -29.32) * mm, v(12.39, -29.73) * mm, v(12.8, -30.26) * mm, v(13.12, -30.9) * mm]});
            skFitSpline(sketch, "E482", {"points": [v(13.12, -30.9) * mm, v(13.45, -31.53) * mm, v(13.66, -32.18) * mm, v(13.76, -32.84) * mm]});
            skFitSpline(sketch, "E483", {"points": [v(13.76, -32.84) * mm, v(13.87, -33.5) * mm, v(13.92, -34.06) * mm, v(13.92, -34.53) * mm]});
            skFitSpline(sketch, "E484", {"points": [v(13.92, -34.53) * mm, v(13.92, -35.58) * mm, v(13.67, -36.1) * mm, v(13.16, -36.1) * mm]});
            skFitSpline(sketch, "E485", {"points": [v(13.16, -36.1) * mm, v(12.73, -36.1) * mm, v(12.1, -35.65) * mm, v(11.28, -34.74) * mm]});
            skFitSpline(sketch, "E486", {"points": [v(10.47, -33.88) * mm, v(10.2, -33.6) * mm, v(10.01, -33.4) * mm, v(9.88, -33.26) * mm]});
            skFitSpline(sketch, "E487", {"points": [v(9.88, -33.26) * mm, v(9.75, -33.12) * mm, v(9.62, -32.94) * mm, v(9.49, -32.74) * mm]});
            skFitSpline(sketch, "E488", {"points": [v(9.49, -32.74) * mm, v(9.35, -32.54) * mm, v(9.28, -32.33) * mm, v(9.28, -32.1) * mm]});
            skFitSpline(sketch, "E489", {"points": [v(9.28, -32.1) * mm, v(9.28, -31.93) * mm, v(9.32, -31.84) * mm, v(9.4, -31.84) * mm]});
            skFitSpline(sketch, "E490", {"points": [v(9.4, -31.84) * mm, v(9.48, -31.84) * mm, v(9.57, -31.9) * mm, v(9.69, -32.05) * mm]});
            skFitSpline(sketch, "E491", {"points": [v(11.14, -33.94) * mm, v(11.65, -34.48) * mm, v(12.02, -34.75) * mm, v(12.27, -34.75) * mm]});
            skFitSpline(sketch, "E492", {"points": [v(12.27, -34.75) * mm, v(12.49, -34.75) * mm, v(12.6, -34.54) * mm, v(12.6, -34.13) * mm]});
            skFitSpline(sketch, "E493", {"points": [v(12.13, -31.6) * mm, v(12.02, -31.02) * mm, v(11.87, -30.55) * mm, v(11.68, -30.21) * mm]});
            skFitSpline(sketch, "E494", {"points": [v(11.68, -30.21) * mm, v(11.5, -29.87) * mm, v(11.29, -29.65) * mm, v(11.07, -29.55) * mm]});
            skFitSpline(sketch, "E495", {"points": [v(11.07, -29.55) * mm, v(10.85, -29.44) * mm, v(10.6, -29.4) * mm, v(10.33, -29.4) * mm]});
            skFitSpline(sketch, "E496", {"points": [v(8.7, -28.7) * mm, v(8.82, -28.7) * mm, v(8.99, -28.7) * mm, v(9.2, -28.7) * mm]});
            skFitSpline(sketch, "E497", {"points": [v(9.2, -28.7) * mm, v(9.37, -28.7) * mm, v(9.46, -28.75) * mm, v(9.46, -28.84) * mm]});
            skFitSpline(sketch, "E498", {"points": [v(10.47, -37.68) * mm, v(10.47, -38.03) * mm, v(10.49, -38.32) * mm, v(10.52, -38.56) * mm]});
            skFitSpline(sketch, "E499", {"points": [v(10.52, -38.56) * mm, v(10.56, -38.8) * mm, v(10.61, -39.05) * mm, v(10.68, -39.3) * mm]});
            skFitSpline(sketch, "E500", {"points": [v(10.68, -39.3) * mm, v(10.78, -39.59) * mm, v(10.95, -39.8) * mm, v(11.18, -39.95) * mm]});
            skFitSpline(sketch, "E501", {"points": [v(11.18, -39.95) * mm, v(11.44, -40.14) * mm, v(11.82, -40.24) * mm, v(12.3, -40.24) * mm]});
            skFitSpline(sketch, "E502", {"points": [v(12.3, -40.24) * mm, v(12.8, -40.24) * mm, v(13.23, -40.1) * mm, v(13.6, -39.8) * mm]});
            skFitSpline(sketch, "E503", {"points": [v(13.6, -39.8) * mm, v(13.97, -39.51) * mm, v(14.15, -39.17) * mm, v(14.15, -38.79) * mm]});
            skFitSpline(sketch, "E504", {"points": [v(14.15, -38.79) * mm, v(14.15, -38.63) * mm, v(14.09, -38.42) * mm, v(13.97, -38.16) * mm]});
            skFitSpline(sketch, "E505", {"points": [v(13.97, -38.16) * mm, v(13.84, -37.9) * mm, v(13.64, -37.65) * mm, v(13.36, -37.43) * mm]});
            skFitSpline(sketch, "E506", {"points": [v(13.36, -37.43) * mm, v(13.09, -37.2) * mm, v(12.88, -37.06) * mm, v(12.75, -36.97) * mm]});
            skFitSpline(sketch, "E507", {"points": [v(12.75, -36.97) * mm, v(12.63, -36.89) * mm, v(12.46, -36.8) * mm, v(12.25, -36.7) * mm]});
            skFitSpline(sketch, "E508", {"points": [v(11.22, -36.28) * mm, v(11.05, -36.22) * mm, v(10.93, -36.17) * mm, v(10.85, -36.13) * mm]});
            skFitSpline(sketch, "E509", {"points": [v(10.85, -36.13) * mm, v(10.78, -36.1) * mm, v(10.71, -36.05) * mm, v(10.66, -36) * mm]});
            skFitSpline(sketch, "E510", {"points": [v(10.7, -35.94) * mm, v(10.92, -35.94) * mm, v(11.3, -36.06) * mm, v(11.84, -36.3) * mm]});
            skFitSpline(sketch, "E511", {"points": [v(11.84, -36.3) * mm, v(12.39, -36.55) * mm, v(12.92, -36.85) * mm, v(13.44, -37.22) * mm]});
            skFitSpline(sketch, "E512", {"points": [v(13.44, -37.22) * mm, v(13.97, -37.58) * mm, v(14.33, -37.93) * mm, v(14.53, -38.26) * mm]});
            skFitSpline(sketch, "E513", {"points": [v(14.53, -38.26) * mm, v(14.73, -38.6) * mm, v(14.83, -39.01) * mm, v(14.83, -39.5) * mm]});
            skFitSpline(sketch, "E514", {"points": [v(14.83, -39.5) * mm, v(14.83, -40) * mm, v(14.68, -40.42) * mm, v(14.4, -40.78) * mm]});
            skFitSpline(sketch, "E515", {"points": [v(14.4, -40.78) * mm, v(14.1, -41.15) * mm, v(13.7, -41.33) * mm, v(13.16, -41.33) * mm]});
            skFitSpline(sketch, "E516", {"points": [v(13.16, -41.33) * mm, v(12.49, -41.33) * mm, v(11.78, -41.05) * mm, v(11.02, -40.5) * mm]});
            skFitSpline(sketch, "E517", {"points": [v(11.02, -40.5) * mm, v(10.26, -39.94) * mm, v(9.75, -39.25) * mm, v(9.49, -38.43) * mm]});
            skFitSpline(sketch, "E518", {"points": [v(9.49, -38.43) * mm, v(9.22, -37.6) * mm, v(9.02, -36.56) * mm, v(8.88, -35.3) * mm]});
            skFitSpline(sketch, "E519", {"points": [v(8.5, -31.75) * mm, v(8.4, -30.62) * mm, v(8.24, -29.7) * mm, v(8.04, -28.95) * mm]});
            skFitSpline(sketch, "E520", {"points": [v(8.04, -28.95) * mm, v(8.04, -28.79) * mm, v(8.26, -28.7) * mm, v(8.7, -28.7) * mm]});
            skFitSpline(sketch, "E521", {"points": [v(2.67, -29.33) * mm, v(2.57, -29.28) * mm, v(2.48, -29.19) * mm, v(2.4, -29.06) * mm]});
            skFitSpline(sketch, "E522", {"points": [v(2.4, -29.06) * mm, v(2.34, -28.94) * mm, v(2.3, -28.82) * mm, v(2.3, -28.72) * mm]});
            skFitSpline(sketch, "E523", {"points": [v(2.3, -28.72) * mm, v(2.3, -28.52) * mm, v(2.5, -28.42) * mm, v(2.88, -28.42) * mm]});
            skFitSpline(sketch, "E524", {"points": [v(4.36, -28.55) * mm, v(4.7, -28.55) * mm, v(5.04, -28.64) * mm, v(5.35, -28.8) * mm]});
            skFitSpline(sketch, "E525", {"points": [v(5.35, -28.8) * mm, v(5.66, -28.96) * mm, v(6, -29.24) * mm, v(6.37, -29.65) * mm]});
            skFitSpline(sketch, "E526", {"points": [v(6.37, -29.65) * mm, v(6.75, -30.06) * mm, v(7.04, -30.54) * mm, v(7.25, -31.09) * mm]});
            skFitSpline(sketch, "E527", {"points": [v(7.25, -31.09) * mm, v(7.45, -31.63) * mm, v(7.6, -32.08) * mm, v(7.7, -32.43) * mm]});
            skFitSpline(sketch, "E528", {"points": [v(7.7, -32.43) * mm, v(7.78, -32.78) * mm, v(7.85, -33.1) * mm, v(7.9, -33.38) * mm]});
            skFitSpline(sketch, "E529", {"points": [v(7.9, -33.38) * mm, v(7.94, -33.67) * mm, v(7.97, -33.9) * mm, v(7.98, -34.1) * mm]});
            skFitSpline(sketch, "E530", {"points": [v(7.98, -34.1) * mm, v(8, -34.28) * mm, v(8, -34.42) * mm, v(8, -34.5) * mm]});
            skFitSpline(sketch, "E531", {"points": [v(8, -34.5) * mm, v(8, -35.53) * mm, v(7.72, -36.04) * mm, v(7.15, -36.04) * mm]});
            skFitSpline(sketch, "E532", {"points": [v(7.15, -36.04) * mm, v(6.62, -36.04) * mm, v(5.88, -35.55) * mm, v(4.94, -34.56) * mm]});
            skFitSpline(sketch, "E533", {"points": [v(4.28, -33.84) * mm, v(4.07, -33.63) * mm, v(3.9, -33.42) * mm, v(3.78, -33.2) * mm]});
            skFitSpline(sketch, "E534", {"points": [v(3.78, -33.2) * mm, v(3.65, -32.97) * mm, v(3.58, -32.75) * mm, v(3.58, -32.53) * mm]});
            skFitSpline(sketch, "E535", {"points": [v(3.58, -32.53) * mm, v(3.58, -32.47) * mm, v(3.6, -32.39) * mm, v(3.66, -32.3) * mm]});
            skFitSpline(sketch, "E536", {"points": [v(4.1, -32.84) * mm, v(4.38, -33.22) * mm, v(4.7, -33.61) * mm, v(5.07, -34) * mm]});
            skFitSpline(sketch, "E537", {"points": [v(5.07, -34) * mm, v(5.45, -34.4) * mm, v(5.77, -34.6) * mm, v(6.04, -34.6) * mm]});
            skFitSpline(sketch, "E538", {"points": [v(6.04, -34.6) * mm, v(6.37, -34.6) * mm, v(6.53, -34.26) * mm, v(6.53, -33.58) * mm]});
            skFitSpline(sketch, "E539", {"points": [v(6.53, -33.58) * mm, v(6.53, -33.1) * mm, v(6.46, -32.5) * mm, v(6.33, -31.8) * mm]});
            skFitSpline(sketch, "E540", {"points": [v(6.33, -31.8) * mm, v(6.19, -31.1) * mm, v(6.03, -30.58) * mm, v(5.86, -30.24) * mm]});
            skFitSpline(sketch, "E541", {"points": [v(5.86, -30.24) * mm, v(5.69, -29.9) * mm, v(5.5, -29.68) * mm, v(5.3, -29.57) * mm]});
            skFitSpline(sketch, "E542", {"points": [v(5.3, -29.57) * mm, v(5.1, -29.46) * mm, v(4.87, -29.4) * mm, v(4.6, -29.4) * mm]});
            skFitSpline(sketch, "E543", {"points": [v(2.19, -29.14) * mm, v(2.19, -28.69) * mm, v(2.33, -28.46) * mm, v(2.62, -28.46) * mm]});
            skFitSpline(sketch, "E544", {"points": [v(2.62, -28.46) * mm, v(2.77, -28.46) * mm, v(2.96, -28.55) * mm, v(3.17, -28.73) * mm]});
            skFitSpline(sketch, "E545", {"points": [v(3.17, -28.73) * mm, v(3.37, -28.93) * mm, v(3.52, -29.18) * mm, v(3.65, -29.48) * mm]});
            skFitSpline(sketch, "E546", {"points": [v(3.65, -29.48) * mm, v(3.77, -29.78) * mm, v(3.86, -30.05) * mm, v(3.9, -30.28) * mm]});
            skFitSpline(sketch, "E547", {"points": [v(3.9, -30.28) * mm, v(3.96, -30.5) * mm, v(4, -30.78) * mm, v(4.02, -31.1) * mm]});
            skFitSpline(sketch, "E548", {"points": [v(4.5, -35.3) * mm, v(4.5, -35.79) * mm, v(4.38, -36.03) * mm, v(4.16, -36.03) * mm]});
            skFitSpline(sketch, "E549", {"points": [v(4.16, -36.03) * mm, v(3.96, -36.03) * mm, v(3.67, -35.88) * mm, v(3.3, -35.6) * mm]});
            skFitSpline(sketch, "E550", {"points": [v(3.3, -35.6) * mm, v(2.95, -35.35) * mm, v(2.36, -34.87) * mm, v(1.54, -34.14) * mm]});
            skFitSpline(sketch, "E551", {"points": [v(1.54, -34.14) * mm, v(1.5, -34.08) * mm, v(1.45, -34.03) * mm, v(1.43, -33.99) * mm]});
            skFitSpline(sketch, "E552", {"points": [v(1.43, -33.99) * mm, v(1.4, -33.95) * mm, v(1.38, -33.91) * mm, v(1.37, -33.87) * mm]});
            skFitSpline(sketch, "E553", {"points": [v(1.37, -33.87) * mm, v(1.37, -33.85) * mm, v(1.4, -33.81) * mm, v(1.47, -33.78) * mm]});
            skFitSpline(sketch, "E554", {"points": [v(1.47, -33.78) * mm, v(1.56, -33.78) * mm, v(1.67, -33.82) * mm, v(1.8, -33.91) * mm]});
            skFitSpline(sketch, "E555", {"points": [v(1.8, -33.91) * mm, v(1.94, -34) * mm, v(2.07, -34.1) * mm, v(2.18, -34.18) * mm]});
            skFitSpline(sketch, "E556", {"points": [v(2.18, -34.18) * mm, v(2.3, -34.27) * mm, v(2.4, -34.36) * mm, v(2.5, -34.45) * mm]});
            skFitSpline(sketch, "E557", {"points": [v(2.9, -34.75) * mm, v(2.92, -34.73) * mm, v(2.93, -34.71) * mm, v(2.95, -34.68) * mm]});
            skFitSpline(sketch, "E558", {"points": [v(2.95, -34.68) * mm, v(2.97, -34.65) * mm, v(2.98, -34.6) * mm, v(2.98, -34.51) * mm]});
            skFitSpline(sketch, "E559", {"points": [v(0.84, -30.58) * mm, v(0.58, -30.28) * mm, v(0.36, -30.13) * mm, v(0.17, -30.13) * mm]});
            skFitSpline(sketch, "E560", {"points": [v(0.17, -30.13) * mm, v(0.01, -30.13) * mm, v(-0.07, -30.34) * mm, v(-0.07, -30.77) * mm]});
            skFitSpline(sketch, "E561", {"points": [v(0.85, -37.11) * mm, v(1.16, -38.88) * mm, v(1.31, -40.07) * mm, v(1.31, -40.66) * mm]});
            skFitSpline(sketch, "E562", {"points": [v(1.31, -40.66) * mm, v(1.31, -41.15) * mm, v(1.2, -41.4) * mm, v(0.96, -41.4) * mm]});
            skFitSpline(sketch, "E563", {"points": [v(0.32, -41.16) * mm, v(0.12, -41.06) * mm, v(-0.05, -40.98) * mm, v(-0.17, -40.93) * mm]});
            skFitSpline(sketch, "E564", {"points": [v(-0.17, -40.93) * mm, v(-0.3, -40.88) * mm, v(-0.44, -40.82) * mm, v(-0.6, -40.76) * mm]});
            skFitSpline(sketch, "E565", {"points": [v(-0.6, -40.76) * mm, v(-0.78, -40.7) * mm, v(-1.03, -40.66) * mm, v(-1.36, -40.66) * mm]});
            skFitSpline(sketch, "E566", {"points": [v(-1.36, -40.66) * mm, v(-1.61, -40.66) * mm, v(-1.73, -40.49) * mm, v(-1.73, -40.14) * mm]});
            skFitSpline(sketch, "E567", {"points": [v(-1.73, -40.14) * mm, v(-1.73, -39.9) * mm, v(-1.62, -39.79) * mm, v(-1.4, -39.79) * mm]});
            skFitSpline(sketch, "E568", {"points": [v(-1.4, -39.79) * mm, v(-1, -40.03) * mm, v(-0.75, -40.16) * mm, v(-0.65, -40.16) * mm]});
            skFitSpline(sketch, "E569", {"points": [v(-0.65, -40.16) * mm, v(-0.5, -40.16) * mm, v(-0.43, -40) * mm, v(-0.43, -39.67) * mm]});
            skFitSpline(sketch, "E570", {"points": [v(-1.62, -29.37) * mm, v(-1.62, -28.8) * mm, v(-1.5, -28.52) * mm, v(-1.25, -28.52) * mm]});
            skFitSpline(sketch, "E571", {"points": [v(-1.25, -28.52) * mm, v(-0.9, -28.52) * mm, v(-0.36, -28.87) * mm, v(0.38, -29.58) * mm]});
            skFitSpline(sketch, "E572", {"points": [v(0.38, -29.58) * mm, v(1.12, -30.28) * mm, v(1.49, -30.7) * mm, v(1.49, -30.85) * mm]});
            skFitSpline(sketch, "E573", {"points": [v(1.49, -30.85) * mm, v(1.49, -30.96) * mm, v(1.44, -31.02) * mm, v(1.35, -31.02) * mm]});
            skFitSpline(sketch, "E574", {"points": [v(1.35, -31.02) * mm, v(1.26, -31.02) * mm, v(1.09, -30.87) * mm, v(0.84, -30.58) * mm]});
            skFitSpline(sketch, "E575", {"points": [v(-0.94, -35.28) * mm, v(-0.83, -35.19) * mm, v(-0.72, -35.14) * mm, v(-0.6, -35.14) * mm]});
            skFitSpline(sketch, "E576", {"points": [v(-0.6, -35.14) * mm, v(-0.53, -35.15) * mm, v(-0.48, -35.19) * mm, v(-0.45, -35.24) * mm]});
            skFitSpline(sketch, "E577", {"points": [v(-0.45, -35.24) * mm, v(-0.43, -35.3) * mm, v(-0.41, -35.36) * mm, v(-0.41, -35.45) * mm]});
            skFitSpline(sketch, "E578", {"points": [v(-0.36, -35.65) * mm, v(-0.24, -35.85) * mm, v(-0.18, -36) * mm, v(-0.18, -36.1) * mm]});
            skFitSpline(sketch, "E579", {"points": [v(-2.27, -36.11) * mm, v(-3.28, -36.11) * mm, v(-3.98, -35.64) * mm, v(-4.35, -34.7) * mm]});
            skFitSpline(sketch, "E580", {"points": [v(-4.35, -34.7) * mm, v(-4.72, -33.76) * mm, v(-4.97, -32.87) * mm, v(-5.1, -32.03) * mm]});
            skFitSpline(sketch, "E581", {"points": [v(-5.1, -32.03) * mm, v(-5.24, -31.2) * mm, v(-5.3, -30.66) * mm, v(-5.32, -30.45) * mm]});
            skFitSpline(sketch, "E582", {"points": [v(-5.32, -30.45) * mm, v(-5.33, -30.24) * mm, v(-5.34, -30.04) * mm, v(-5.34, -29.84) * mm]});
            skFitSpline(sketch, "E583", {"points": [v(-5.34, -29.84) * mm, v(-5.34, -28.94) * mm, v(-5.11, -28.49) * mm, v(-4.66, -28.49) * mm]});
            skFitSpline(sketch, "E584", {"points": [v(-4.66, -28.49) * mm, v(-4.2, -28.49) * mm, v(-3.5, -29) * mm, v(-2.53, -30.03) * mm]});
            skFitSpline(sketch, "E585", {"points": [v(-1.85, -30.67) * mm, v(-1.51, -30.98) * mm, v(-1.27, -31.23) * mm, v(-1.13, -31.41) * mm]});
            skFitSpline(sketch, "E586", {"points": [v(-1.13, -31.41) * mm, v(-0.99, -31.6) * mm, v(-0.92, -31.79) * mm, v(-0.92, -32) * mm]});
            skFitSpline(sketch, "E587", {"points": [v(-0.92, -32) * mm, v(-0.92, -32.05) * mm, v(-0.95, -32.1) * mm, v(-1.02, -32.17) * mm]});
            skFitSpline(sketch, "E588", {"points": [v(-1.02, -32.17) * mm, v(-1.18, -32.17) * mm, v(-1.58, -31.8) * mm, v(-2.22, -31.05) * mm]});
            skFitSpline(sketch, "E589", {"points": [v(-2.22, -31.05) * mm, v(-2.76, -30.47) * mm, v(-3.17, -30.18) * mm, v(-3.44, -30.18) * mm]});
            skFitSpline(sketch, "E590", {"points": [v(-3.44, -30.18) * mm, v(-3.72, -30.18) * mm, v(-3.87, -30.47) * mm, v(-3.87, -31.07) * mm]});
            skFitSpline(sketch, "E591", {"points": [v(-3.87, -31.07) * mm, v(-3.87, -31.6) * mm, v(-3.78, -32.28) * mm, v(-3.6, -33.1) * mm]});
            skFitSpline(sketch, "E592", {"points": [v(-3.6, -33.1) * mm, v(-3.43, -33.93) * mm, v(-3.2, -34.56) * mm, v(-2.94, -35) * mm]});
            skFitSpline(sketch, "E593", {"points": [v(-2.94, -35) * mm, v(-2.68, -35.43) * mm, v(-2.37, -35.65) * mm, v(-2, -35.65) * mm]});
            skFitSpline(sketch, "E594", {"points": [v(-2, -35.65) * mm, v(-1.7, -35.65) * mm, v(-1.34, -35.52) * mm, v(-0.94, -35.28) * mm]});
            skFitSpline(sketch, "E595", {"points": [v(-10.8, -29.33) * mm, v(-10.91, -29.28) * mm, v(-11, -29.19) * mm, v(-11.07, -29.06) * mm]});
            skFitSpline(sketch, "E596", {"points": [v(-11.07, -29.06) * mm, v(-11.14, -28.94) * mm, v(-11.18, -28.82) * mm, v(-11.18, -28.72) * mm]});
            skFitSpline(sketch, "E597", {"points": [v(-11.18, -28.72) * mm, v(-11.18, -28.52) * mm, v(-10.98, -28.42) * mm, v(-10.6, -28.42) * mm]});
            skFitSpline(sketch, "E598", {"points": [v(-9.12, -28.55) * mm, v(-8.77, -28.55) * mm, v(-8.44, -28.64) * mm, v(-8.13, -28.8) * mm]});
            skFitSpline(sketch, "E599", {"points": [v(-8.13, -28.8) * mm, v(-7.82, -28.96) * mm, v(-7.48, -29.24) * mm, v(-7.1, -29.65) * mm]});
            skFitSpline(sketch, "E600", {"points": [v(-7.1, -29.65) * mm, v(-6.73, -30.06) * mm, v(-6.44, -30.54) * mm, v(-6.23, -31.09) * mm]});
            skFitSpline(sketch, "E601", {"points": [v(-6.23, -31.09) * mm, v(-6.03, -31.63) * mm, v(-5.88, -32.08) * mm, v(-5.79, -32.43) * mm]});
            skFitSpline(sketch, "E602", {"points": [v(-5.79, -32.43) * mm, v(-5.7, -32.78) * mm, v(-5.63, -33.1) * mm, v(-5.58, -33.38) * mm]});
            skFitSpline(sketch, "E603", {"points": [v(-5.58, -33.38) * mm, v(-5.54, -33.67) * mm, v(-5.5, -33.9) * mm, v(-5.5, -34.1) * mm]});
            skFitSpline(sketch, "E604", {"points": [v(-5.5, -34.1) * mm, v(-5.48, -34.28) * mm, v(-5.48, -34.42) * mm, v(-5.48, -34.5) * mm]});
            skFitSpline(sketch, "E605", {"points": [v(-5.48, -34.5) * mm, v(-5.48, -35.53) * mm, v(-5.76, -36.04) * mm, v(-6.33, -36.04) * mm]});
            skFitSpline(sketch, "E606", {"points": [v(-6.33, -36.04) * mm, v(-6.86, -36.04) * mm, v(-7.6, -35.55) * mm, v(-8.54, -34.56) * mm]});
            skFitSpline(sketch, "E607", {"points": [v(-9.2, -33.84) * mm, v(-9.4, -33.63) * mm, v(-9.57, -33.42) * mm, v(-9.7, -33.2) * mm]});
            skFitSpline(sketch, "E608", {"points": [v(-9.7, -33.2) * mm, v(-9.83, -32.97) * mm, v(-9.9, -32.75) * mm, v(-9.9, -32.53) * mm]});
            skFitSpline(sketch, "E609", {"points": [v(-9.9, -32.53) * mm, v(-9.9, -32.47) * mm, v(-9.87, -32.39) * mm, v(-9.82, -32.3) * mm]});
            skFitSpline(sketch, "E610", {"points": [v(-9.37, -32.84) * mm, v(-9.1, -33.22) * mm, v(-8.78, -33.61) * mm, v(-8.4, -34) * mm]});
            skFitSpline(sketch, "E611", {"points": [v(-8.4, -34) * mm, v(-8.03, -34.4) * mm, v(-7.7, -34.6) * mm, v(-7.43, -34.6) * mm]});
            skFitSpline(sketch, "E612", {"points": [v(-7.43, -34.6) * mm, v(-7.11, -34.6) * mm, v(-6.95, -34.26) * mm, v(-6.95, -33.58) * mm]});
            skFitSpline(sketch, "E613", {"points": [v(-6.95, -33.58) * mm, v(-6.95, -33.1) * mm, v(-7.02, -32.5) * mm, v(-7.15, -31.8) * mm]});
            skFitSpline(sketch, "E614", {"points": [v(-7.15, -31.8) * mm, v(-7.29, -31.1) * mm, v(-7.44, -30.58) * mm, v(-7.62, -30.24) * mm]});
            skFitSpline(sketch, "E615", {"points": [v(-7.62, -30.24) * mm, v(-7.8, -29.9) * mm, v(-7.98, -29.68) * mm, v(-8.18, -29.57) * mm]});
            skFitSpline(sketch, "E616", {"points": [v(-8.18, -29.57) * mm, v(-8.38, -29.46) * mm, v(-8.61, -29.4) * mm, v(-8.87, -29.4) * mm]});
            skFitSpline(sketch, "E617", {"points": [v(-11.29, -29.14) * mm, v(-11.29, -28.69) * mm, v(-11.15, -28.46) * mm, v(-10.86, -28.46) * mm]});
            skFitSpline(sketch, "E618", {"points": [v(-10.86, -28.46) * mm, v(-10.7, -28.46) * mm, v(-10.52, -28.55) * mm, v(-10.3, -28.73) * mm]});
            skFitSpline(sketch, "E619", {"points": [v(-10.3, -28.73) * mm, v(-10.11, -28.93) * mm, v(-9.95, -29.18) * mm, v(-9.83, -29.48) * mm]});
            skFitSpline(sketch, "E620", {"points": [v(-9.83, -29.48) * mm, v(-9.7, -29.78) * mm, v(-9.62, -30.05) * mm, v(-9.57, -30.28) * mm]});
            skFitSpline(sketch, "E621", {"points": [v(-9.57, -30.28) * mm, v(-9.52, -30.5) * mm, v(-9.48, -30.78) * mm, v(-9.46, -31.1) * mm]});
            skFitSpline(sketch, "E622", {"points": [v(-8.99, -35.3) * mm, v(-8.99, -35.79) * mm, v(-9.1, -36.03) * mm, v(-9.32, -36.03) * mm]});
            skFitSpline(sketch, "E623", {"points": [v(-9.32, -36.03) * mm, v(-9.52, -36.03) * mm, v(-9.8, -35.88) * mm, v(-10.17, -35.6) * mm]});
            skFitSpline(sketch, "E624", {"points": [v(-10.17, -35.6) * mm, v(-10.53, -35.35) * mm, v(-11.12, -34.87) * mm, v(-11.93, -34.14) * mm]});
            skFitSpline(sketch, "E625", {"points": [v(-11.93, -34.14) * mm, v(-11.99, -34.08) * mm, v(-12.02, -34.03) * mm, v(-12.05, -33.99) * mm]});
            skFitSpline(sketch, "E626", {"points": [v(-12.05, -33.99) * mm, v(-12.08, -33.95) * mm, v(-12.1, -33.91) * mm, v(-12.1, -33.87) * mm]});
            skFitSpline(sketch, "E627", {"points": [v(-12.1, -33.87) * mm, v(-12.1, -33.85) * mm, v(-12.08, -33.81) * mm, v(-12.01, -33.78) * mm]});
            skFitSpline(sketch, "E628", {"points": [v(-12.01, -33.78) * mm, v(-11.92, -33.78) * mm, v(-11.8, -33.82) * mm, v(-11.67, -33.91) * mm]});
            skFitSpline(sketch, "E629", {"points": [v(-11.67, -33.91) * mm, v(-11.54, -34) * mm, v(-11.41, -34.1) * mm, v(-11.3, -34.18) * mm]});
            skFitSpline(sketch, "E630", {"points": [v(-11.3, -34.18) * mm, v(-11.18, -34.27) * mm, v(-11.07, -34.36) * mm, v(-10.98, -34.45) * mm]});
            skFitSpline(sketch, "E631", {"points": [v(-10.58, -34.75) * mm, v(-10.56, -34.73) * mm, v(-10.55, -34.71) * mm, v(-10.53, -34.68) * mm]});
            skFitSpline(sketch, "E632", {"points": [v(-10.53, -34.68) * mm, v(-10.5, -34.65) * mm, v(-10.5, -34.6) * mm, v(-10.5, -34.51) * mm]});
            skFitSpline(sketch, "E633", {"points": [v(-15.04, -33.96) * mm, v(-14.75, -34.25) * mm, v(-14.54, -34.4) * mm, v(-14.4, -34.4) * mm]});
            skFitSpline(sketch, "E634", {"points": [v(-14.4, -34.4) * mm, v(-14.24, -34.4) * mm, v(-14.16, -34.18) * mm, v(-14.16, -33.74) * mm]});
            skFitSpline(sketch, "E635", {"points": [v(-15.08, -27.43) * mm, v(-15.46, -25.24) * mm, v(-15.66, -23.89) * mm, v(-15.66, -23.38) * mm]});
            skFitSpline(sketch, "E636", {"points": [v(-15.66, -23.38) * mm, v(-15.66, -22.98) * mm, v(-15.57, -22.78) * mm, v(-15.39, -22.78) * mm]});
            skFitSpline(sketch, "E637", {"points": [v(-15.39, -22.78) * mm, v(-15.26, -22.78) * mm, v(-15.13, -22.83) * mm, v(-15, -22.92) * mm]});
            skFitSpline(sketch, "E638", {"points": [v(-14.03, -23.56) * mm, v(-13.56, -23.88) * mm, v(-13.19, -24.12) * mm, v(-12.9, -24.28) * mm]});
            skFitSpline(sketch, "E639", {"points": [v(-12.9, -24.28) * mm, v(-12.62, -24.44) * mm, v(-12.48, -24.6) * mm, v(-12.48, -24.72) * mm]});
            skFitSpline(sketch, "E640", {"points": [v(-12.48, -24.72) * mm, v(-12.5, -24.82) * mm, v(-12.55, -24.87) * mm, v(-12.63, -24.87) * mm]});
            skFitSpline(sketch, "E641", {"points": [v(-12.86, -24.8) * mm, v(-13.36, -24.5) * mm, v(-13.64, -24.35) * mm, v(-13.72, -24.35) * mm]});
            skFitSpline(sketch, "E642", {"points": [v(-13.72, -24.35) * mm, v(-13.85, -24.35) * mm, v(-13.91, -24.49) * mm, v(-13.91, -24.76) * mm]});
            skFitSpline(sketch, "E643", {"points": [v(-12.55, -35.39) * mm, v(-12.55, -35.9) * mm, v(-12.67, -36.16) * mm, v(-12.9, -36.16) * mm]});
            skFitSpline(sketch, "E644", {"points": [v(-12.9, -36.16) * mm, v(-13.25, -36.16) * mm, v(-13.82, -35.77) * mm, v(-14.6, -35) * mm]});
            skFitSpline(sketch, "E645", {"points": [v(-14.6, -35) * mm, v(-15.37, -34.22) * mm, v(-15.75, -33.78) * mm, v(-15.75, -33.66) * mm]});
            skFitSpline(sketch, "E646", {"points": [v(-15.75, -33.66) * mm, v(-15.75, -33.57) * mm, v(-15.7, -33.52) * mm, v(-15.6, -33.52) * mm]});
            skFitSpline(sketch, "E647", {"points": [v(-15.6, -33.52) * mm, v(-15.5, -33.52) * mm, v(-15.32, -33.67) * mm, v(-15.04, -33.96) * mm]});
            skFitSpline(sketch, "E648", {"points": [v(-18.37, -28.75) * mm, v(-17.76, -28.96) * mm, v(-17.33, -29.2) * mm, v(-17.05, -29.48) * mm]});
            skFitSpline(sketch, "E649", {"points": [v(-17.05, -29.48) * mm, v(-16.78, -29.75) * mm, v(-16.52, -30.34) * mm, v(-16.26, -31.23) * mm]});
            skFitSpline(sketch, "E650", {"points": [v(-16.26, -31.23) * mm, v(-16, -32.12) * mm, v(-15.87, -32.85) * mm, v(-15.87, -33.43) * mm]});
            skFitSpline(sketch, "E651", {"points": [v(-15.87, -33.43) * mm, v(-15.87, -34.16) * mm, v(-16.02, -34.78) * mm, v(-16.32, -35.3) * mm]});
            skFitSpline(sketch, "E652", {"points": [v(-16.32, -35.3) * mm, v(-16.61, -35.8) * mm, v(-17.03, -36.06) * mm, v(-17.56, -36.06) * mm]});
            skFitSpline(sketch, "E653", {"points": [v(-17.56, -36.06) * mm, v(-18.1, -36.06) * mm, v(-18.62, -35.9) * mm, v(-19.13, -35.54) * mm]});
            skFitSpline(sketch, "E654", {"points": [v(-20.12, -34.9) * mm, v(-20.3, -34.79) * mm, v(-20.45, -34.68) * mm, v(-20.58, -34.57) * mm]});
            skFitSpline(sketch, "E655", {"points": [v(-20.58, -34.57) * mm, v(-20.71, -34.46) * mm, v(-20.84, -34.34) * mm, v(-20.97, -34.2) * mm]});
            skFitSpline(sketch, "E656", {"points": [v(-20.97, -34.2) * mm, v(-21.1, -34.08) * mm, v(-21.2, -33.86) * mm, v(-21.26, -33.55) * mm]});
            skFitSpline(sketch, "E657", {"points": [v(-21.79, -30.84) * mm, v(-21.79, -30.26) * mm, v(-21.54, -29.7) * mm, v(-21.06, -29.17) * mm]});
            skFitSpline(sketch, "E658", {"points": [v(-21.06, -29.17) * mm, v(-20.57, -28.63) * mm, v(-20.16, -28.37) * mm, v(-19.8, -28.37) * mm]});
            skFitSpline(sketch, "E659", {"points": [v(-18, -30.05) * mm, v(-18.1, -29.8) * mm, v(-18.2, -29.6) * mm, v(-18.3, -29.45) * mm]});
            skFitSpline(sketch, "E660", {"points": [v(-18.3, -29.45) * mm, v(-18.42, -29.32) * mm, v(-18.52, -29.24) * mm, v(-18.58, -29.2) * mm]});
            skFitSpline(sketch, "E661", {"points": [v(-18.58, -29.2) * mm, v(-18.63, -29.16) * mm, v(-18.7, -29.11) * mm, v(-18.79, -29.05) * mm]});
            skFitSpline(sketch, "E662", {"points": [v(-18.79, -29.05) * mm, v(-18.87, -29) * mm, v(-18.97, -28.97) * mm, v(-19.1, -28.97) * mm]});
            skFitSpline(sketch, "E663", {"points": [v(-19.1, -28.97) * mm, v(-19.3, -28.97) * mm, v(-19.5, -29.07) * mm, v(-19.68, -29.29) * mm]});
            skFitSpline(sketch, "E664", {"points": [v(-19.68, -29.29) * mm, v(-19.86, -29.5) * mm, v(-19.96, -29.73) * mm, v(-20, -29.97) * mm]});
            skFitSpline(sketch, "E665", {"points": [v(-20, -29.97) * mm, v(-20.1, -30.43) * mm, v(-20.16, -30.87) * mm, v(-20.16, -31.31) * mm]});
            skFitSpline(sketch, "E666", {"points": [v(-20.16, -31.31) * mm, v(-20.16, -32.05) * mm, v(-20.07, -32.74) * mm, v(-19.9, -33.39) * mm]});
            skFitSpline(sketch, "E667", {"points": [v(-19.9, -33.39) * mm, v(-19.74, -34.03) * mm, v(-19.53, -34.46) * mm, v(-19.3, -34.68) * mm]});
            skFitSpline(sketch, "E668", {"points": [v(-19.3, -34.68) * mm, v(-19.05, -34.9) * mm, v(-18.89, -35) * mm, v(-18.8, -35) * mm]});
            skFitSpline(sketch, "E669", {"points": [v(-18.8, -35) * mm, v(-18.64, -35) * mm, v(-18.45, -34.92) * mm, v(-18.2, -34.77) * mm]});
            skFitSpline(sketch, "E670", {"points": [v(-18.2, -34.77) * mm, v(-17.97, -34.61) * mm, v(-17.78, -34.33) * mm, v(-17.65, -33.91) * mm]});
            skFitSpline(sketch, "E671", {"points": [v(-17.65, -33.91) * mm, v(-17.5, -33.5) * mm, v(-17.44, -33.04) * mm, v(-17.44, -32.53) * mm]});
            skFitSpline(sketch, "E672", {"points": [v(-17.44, -32.53) * mm, v(-17.44, -32.15) * mm, v(-17.47, -31.86) * mm, v(-17.54, -31.66) * mm]});
            skFitSpline(sketch, "E673", {"points": [v(-24.75, -28.75) * mm, v(-24.15, -28.96) * mm, v(-23.7, -29.2) * mm, v(-23.43, -29.48) * mm]});
            skFitSpline(sketch, "E674", {"points": [v(-23.43, -29.48) * mm, v(-23.16, -29.75) * mm, v(-22.9, -30.34) * mm, v(-22.64, -31.23) * mm]});
            skFitSpline(sketch, "E675", {"points": [v(-22.64, -31.23) * mm, v(-22.38, -32.12) * mm, v(-22.25, -32.85) * mm, v(-22.25, -33.43) * mm]});
            skFitSpline(sketch, "E676", {"points": [v(-22.25, -33.43) * mm, v(-22.25, -34.16) * mm, v(-22.4, -34.78) * mm, v(-22.7, -35.3) * mm]});
            skFitSpline(sketch, "E677", {"points": [v(-22.7, -35.3) * mm, v(-23, -35.8) * mm, v(-23.4, -36.06) * mm, v(-23.94, -36.06) * mm]});
            skFitSpline(sketch, "E678", {"points": [v(-23.94, -36.06) * mm, v(-24.48, -36.06) * mm, v(-25, -35.9) * mm, v(-25.5, -35.54) * mm]});
            skFitSpline(sketch, "E679", {"points": [v(-26.5, -34.9) * mm, v(-26.68, -34.79) * mm, v(-26.83, -34.68) * mm, v(-26.96, -34.57) * mm]});
            skFitSpline(sketch, "E680", {"points": [v(-26.96, -34.57) * mm, v(-27.1, -34.46) * mm, v(-27.22, -34.34) * mm, v(-27.35, -34.2) * mm]});
            skFitSpline(sketch, "E681", {"points": [v(-27.35, -34.2) * mm, v(-27.48, -34.08) * mm, v(-27.58, -33.86) * mm, v(-27.64, -33.55) * mm]});
            skFitSpline(sketch, "E682", {"points": [v(-28.17, -30.84) * mm, v(-28.17, -30.26) * mm, v(-27.92, -29.7) * mm, v(-27.44, -29.17) * mm]});
            skFitSpline(sketch, "E683", {"points": [v(-27.44, -29.17) * mm, v(-26.95, -28.63) * mm, v(-26.54, -28.37) * mm, v(-26.19, -28.37) * mm]});
            skFitSpline(sketch, "E684", {"points": [v(-24.38, -30.05) * mm, v(-24.48, -29.8) * mm, v(-24.57, -29.6) * mm, v(-24.68, -29.45) * mm]});
            skFitSpline(sketch, "E685", {"points": [v(-24.68, -29.45) * mm, v(-24.8, -29.32) * mm, v(-24.9, -29.24) * mm, v(-24.96, -29.2) * mm]});
            skFitSpline(sketch, "E686", {"points": [v(-24.96, -29.2) * mm, v(-25.02, -29.16) * mm, v(-25.09, -29.11) * mm, v(-25.17, -29.05) * mm]});
            skFitSpline(sketch, "E687", {"points": [v(-25.17, -29.05) * mm, v(-25.25, -29) * mm, v(-25.35, -28.97) * mm, v(-25.47, -28.97) * mm]});
            skFitSpline(sketch, "E688", {"points": [v(-25.47, -28.97) * mm, v(-25.7, -28.97) * mm, v(-25.89, -29.07) * mm, v(-26.06, -29.29) * mm]});
            skFitSpline(sketch, "E689", {"points": [v(-26.06, -29.29) * mm, v(-26.24, -29.5) * mm, v(-26.34, -29.73) * mm, v(-26.38, -29.97) * mm]});
            skFitSpline(sketch, "E690", {"points": [v(-26.38, -29.97) * mm, v(-26.49, -30.43) * mm, v(-26.54, -30.87) * mm, v(-26.54, -31.31) * mm]});
            skFitSpline(sketch, "E691", {"points": [v(-26.54, -31.31) * mm, v(-26.54, -32.05) * mm, v(-26.45, -32.74) * mm, v(-26.29, -33.39) * mm]});
            skFitSpline(sketch, "E692", {"points": [v(-26.29, -33.39) * mm, v(-26.12, -34.03) * mm, v(-25.91, -34.46) * mm, v(-25.67, -34.68) * mm]});
            skFitSpline(sketch, "E693", {"points": [v(-25.67, -34.68) * mm, v(-25.43, -34.9) * mm, v(-25.27, -35) * mm, v(-25.18, -35) * mm]});
            skFitSpline(sketch, "E694", {"points": [v(-25.18, -35) * mm, v(-25.02, -35) * mm, v(-24.83, -34.92) * mm, v(-24.59, -34.77) * mm]});
            skFitSpline(sketch, "E695", {"points": [v(-24.59, -34.77) * mm, v(-24.35, -34.61) * mm, v(-24.16, -34.33) * mm, v(-24.03, -33.91) * mm]});
            skFitSpline(sketch, "E696", {"points": [v(-24.03, -33.91) * mm, v(-23.9, -33.5) * mm, v(-23.82, -33.04) * mm, v(-23.82, -32.53) * mm]});
            skFitSpline(sketch, "E697", {"points": [v(-23.82, -32.53) * mm, v(-23.82, -32.15) * mm, v(-23.85, -31.86) * mm, v(-23.92, -31.66) * mm]});
            skFitSpline(sketch, "E698", {"points": [v(-29.49, -30.2) * mm, v(-29.52, -29.94) * mm, v(-29.64, -29.77) * mm, v(-29.82, -29.71) * mm]});
            skFitSpline(sketch, "E699", {"points": [v(-29.82, -29.71) * mm, v(-30.01, -29.65) * mm, v(-30.34, -29.63) * mm, v(-30.82, -29.63) * mm]});
            skFitSpline(sketch, "E700", {"points": [v(-32.6, -29.59) * mm, v(-32.3, -30.26) * mm, v(-31.89, -31) * mm, v(-31.38, -31.82) * mm]});
            skFitSpline(sketch, "E701", {"points": [v(-31.38, -31.82) * mm, v(-30.87, -32.63) * mm, v(-30.37, -33.32) * mm, v(-29.9, -33.87) * mm]});
            skFitSpline(sketch, "E702", {"points": [v(-29.9, -33.87) * mm, v(-29.43, -34.43) * mm, v(-28.81, -35.04) * mm, v(-28.05, -35.7) * mm]});
            skFitSpline(sketch, "E703", {"points": [v(-28.34, -36) * mm, v(-28.77, -35.68) * mm, v(-29.35, -35.2) * mm, v(-30.1, -34.53) * mm]});
            skFitSpline(sketch, "E704", {"points": [v(-30.1, -34.53) * mm, v(-30.84, -33.87) * mm, v(-31.53, -33.1) * mm, v(-32.16, -32.19) * mm]});
            skFitSpline(sketch, "E705", {"points": [v(-34.28, -28.64) * mm, v(-34.3, -28.6) * mm, v(-34.31, -28.54) * mm, v(-34.31, -28.46) * mm]});
            skFitSpline(sketch, "E706", {"points": [v(-34.31, -28.46) * mm, v(-34.31, -28.37) * mm, v(-34.27, -28.33) * mm, v(-34.18, -28.33) * mm]});
            skFitSpline(sketch, "E707", {"points": [v(-34.02, -28.38) * mm, v(-33.87, -28.5) * mm, v(-33.58, -28.56) * mm, v(-33.17, -28.56) * mm]});
            skFitSpline(sketch, "E708", {"points": [v(-30.4, -28.23) * mm, v(-30.06, -28.23) * mm, v(-29.8, -28.29) * mm, v(-29.6, -28.4) * mm]});
            skFitSpline(sketch, "E709", {"points": [v(-29.6, -28.4) * mm, v(-29.4, -28.52) * mm, v(-29.28, -28.65) * mm, v(-29.22, -28.8) * mm]});
            skFitSpline(sketch, "E710", {"points": [v(-29.22, -28.8) * mm, v(-29.17, -28.93) * mm, v(-29.12, -29.12) * mm, v(-29.1, -29.33) * mm]});
            skFitSpline(sketch, "E711", {"points": [v(-29.02, -30) * mm, v(-29.02, -30.4) * mm, v(-29.1, -30.61) * mm, v(-29.23, -30.61) * mm]});
            skFitSpline(sketch, "E712", {"points": [v(-29.23, -30.61) * mm, v(-29.36, -30.61) * mm, v(-29.45, -30.48) * mm, v(-29.49, -30.2) * mm]});
            skFitSpline(sketch, "E713", {"points": [v(-28.22, -35.85) * mm, v(-28.25, -35.88) * mm, v(-28.3, -35.9) * mm, v(-28.4, -35.95) * mm]});
            skFitSpline(sketch, "E714", {"points": [v(-29.27, -35.27) * mm, v(-29.45, -35.15) * mm, v(-29.62, -35.1) * mm, v(-29.78, -35.1) * mm]});
            skFitSpline(sketch, "E715", {"points": [v(-29.78, -35.1) * mm, v(-30.02, -35.1) * mm, v(-30.42, -35.3) * mm, v(-30.96, -35.68) * mm]});
            skFitSpline(sketch, "E716", {"points": [v(-30.96, -35.68) * mm, v(-31.27, -35.94) * mm, v(-31.63, -36.06) * mm, v(-32.03, -36.06) * mm]});
            skFitSpline(sketch, "E717", {"points": [v(-32.03, -36.06) * mm, v(-32.43, -36.06) * mm, v(-32.81, -35.93) * mm, v(-33.19, -35.66) * mm]});
            skFitSpline(sketch, "E718", {"points": [v(-33.19, -35.66) * mm, v(-33.56, -35.4) * mm, v(-33.83, -35.1) * mm, v(-33.98, -34.79) * mm]});
            skFitSpline(sketch, "E719", {"points": [v(-33.98, -34.79) * mm, v(-34.14, -34.47) * mm, v(-34.22, -34.25) * mm, v(-34.22, -34.12) * mm]});
            skFitSpline(sketch, "E720", {"points": [v(-34.22, -34.12) * mm, v(-34.22, -34.07) * mm, v(-34.19, -34.02) * mm, v(-34.12, -33.97) * mm]});
            skFitSpline(sketch, "E721", {"points": [v(-34.12, -33.97) * mm, v(-34, -33.97) * mm, v(-33.9, -34.05) * mm, v(-33.83, -34.22) * mm]});
            skFitSpline(sketch, "E722", {"points": [v(-33.83, -34.22) * mm, v(-33.56, -34.62) * mm, v(-33.23, -34.82) * mm, v(-32.84, -34.82) * mm]});
            skFitSpline(sketch, "E723", {"points": [v(-32.84, -34.82) * mm, v(-32.71, -34.82) * mm, v(-32.6, -34.81) * mm, v(-32.48, -34.78) * mm]});
            skFitSpline(sketch, "E724", {"points": [v(-32.48, -34.78) * mm, v(-32.37, -34.76) * mm, v(-32.25, -34.72) * mm, v(-32.12, -34.67) * mm]});
            skFitSpline(sketch, "E725", {"points": [v(-30.22, -33.8) * mm, v(-30.1, -33.74) * mm, v(-29.98, -33.72) * mm, v(-29.83, -33.72) * mm]});
            skFitSpline(sketch, "E726", {"points": [v(-29.83, -33.72) * mm, v(-29.5, -33.72) * mm, v(-29.2, -33.86) * mm, v(-28.91, -34.13) * mm]});
            skFitSpline(sketch, "E727", {"points": [v(-28.91, -34.13) * mm, v(-28.64, -34.41) * mm, v(-28.45, -34.73) * mm, v(-28.36, -35.08) * mm]});
            skFitSpline(sketch, "E728", {"points": [v(-39.76, -29.33) * mm, v(-39.87, -29.28) * mm, v(-39.95, -29.19) * mm, v(-40.03, -29.06) * mm]});
            skFitSpline(sketch, "E729", {"points": [v(-40.03, -29.06) * mm, v(-40.1, -28.94) * mm, v(-40.13, -28.82) * mm, v(-40.13, -28.72) * mm]});
            skFitSpline(sketch, "E730", {"points": [v(-40.13, -28.72) * mm, v(-40.13, -28.52) * mm, v(-39.94, -28.42) * mm, v(-39.55, -28.42) * mm]});
            skFitSpline(sketch, "E731", {"points": [v(-38.08, -28.55) * mm, v(-37.73, -28.55) * mm, v(-37.4, -28.64) * mm, v(-37.09, -28.8) * mm]});
            skFitSpline(sketch, "E732", {"points": [v(-37.09, -28.8) * mm, v(-36.78, -28.96) * mm, v(-36.43, -29.24) * mm, v(-36.06, -29.65) * mm]});
            skFitSpline(sketch, "E733", {"points": [v(-36.06, -29.65) * mm, v(-35.68, -30.06) * mm, v(-35.4, -30.54) * mm, v(-35.19, -31.09) * mm]});
            skFitSpline(sketch, "E734", {"points": [v(-35.19, -31.09) * mm, v(-34.98, -31.63) * mm, v(-34.83, -32.08) * mm, v(-34.74, -32.43) * mm]});
            skFitSpline(sketch, "E735", {"points": [v(-34.74, -32.43) * mm, v(-34.65, -32.78) * mm, v(-34.58, -33.1) * mm, v(-34.54, -33.38) * mm]});
            skFitSpline(sketch, "E736", {"points": [v(-34.54, -33.38) * mm, v(-34.5, -33.67) * mm, v(-34.46, -33.9) * mm, v(-34.45, -34.1) * mm]});
            skFitSpline(sketch, "E737", {"points": [v(-34.45, -34.1) * mm, v(-34.44, -34.28) * mm, v(-34.43, -34.42) * mm, v(-34.43, -34.5) * mm]});
            skFitSpline(sketch, "E738", {"points": [v(-34.43, -34.5) * mm, v(-34.43, -35.53) * mm, v(-34.71, -36.04) * mm, v(-35.28, -36.04) * mm]});
            skFitSpline(sketch, "E739", {"points": [v(-35.28, -36.04) * mm, v(-35.81, -36.04) * mm, v(-36.55, -35.55) * mm, v(-37.5, -34.56) * mm]});
            skFitSpline(sketch, "E740", {"points": [v(-38.15, -33.84) * mm, v(-38.36, -33.63) * mm, v(-38.53, -33.42) * mm, v(-38.66, -33.2) * mm]});
            skFitSpline(sketch, "E741", {"points": [v(-38.66, -33.2) * mm, v(-38.79, -32.97) * mm, v(-38.85, -32.75) * mm, v(-38.85, -32.53) * mm]});
            skFitSpline(sketch, "E742", {"points": [v(-38.85, -32.53) * mm, v(-38.85, -32.47) * mm, v(-38.83, -32.39) * mm, v(-38.77, -32.3) * mm]});
            skFitSpline(sketch, "E743", {"points": [v(-38.33, -32.84) * mm, v(-38.06, -33.22) * mm, v(-37.73, -33.61) * mm, v(-37.36, -34) * mm]});
            skFitSpline(sketch, "E744", {"points": [v(-37.36, -34) * mm, v(-36.98, -34.4) * mm, v(-36.66, -34.6) * mm, v(-36.39, -34.6) * mm]});
            skFitSpline(sketch, "E745", {"points": [v(-36.39, -34.6) * mm, v(-36.07, -34.6) * mm, v(-35.9, -34.26) * mm, v(-35.9, -33.58) * mm]});
            skFitSpline(sketch, "E746", {"points": [v(-35.9, -33.58) * mm, v(-35.9, -33.1) * mm, v(-35.97, -32.5) * mm, v(-36.1, -31.8) * mm]});
            skFitSpline(sketch, "E747", {"points": [v(-36.1, -31.8) * mm, v(-36.24, -31.1) * mm, v(-36.4, -30.58) * mm, v(-36.57, -30.24) * mm]});
            skFitSpline(sketch, "E748", {"points": [v(-36.57, -30.24) * mm, v(-36.75, -29.9) * mm, v(-36.94, -29.68) * mm, v(-37.14, -29.57) * mm]});
            skFitSpline(sketch, "E749", {"points": [v(-37.14, -29.57) * mm, v(-37.34, -29.46) * mm, v(-37.57, -29.4) * mm, v(-37.82, -29.4) * mm]});
            skFitSpline(sketch, "E750", {"points": [v(-40.24, -29.14) * mm, v(-40.24, -28.69) * mm, v(-40.1, -28.46) * mm, v(-39.82, -28.46) * mm]});
            skFitSpline(sketch, "E751", {"points": [v(-39.82, -28.46) * mm, v(-39.66, -28.46) * mm, v(-39.48, -28.55) * mm, v(-39.26, -28.73) * mm]});
            skFitSpline(sketch, "E752", {"points": [v(-39.26, -28.73) * mm, v(-39.07, -28.93) * mm, v(-38.9, -29.18) * mm, v(-38.79, -29.48) * mm]});
            skFitSpline(sketch, "E753", {"points": [v(-38.79, -29.48) * mm, v(-38.66, -29.78) * mm, v(-38.58, -30.05) * mm, v(-38.53, -30.28) * mm]});
            skFitSpline(sketch, "E754", {"points": [v(-38.53, -30.28) * mm, v(-38.47, -30.5) * mm, v(-38.44, -30.78) * mm, v(-38.41, -31.1) * mm]});
            skFitSpline(sketch, "E755", {"points": [v(-37.94, -35.3) * mm, v(-37.94, -35.79) * mm, v(-38.05, -36.03) * mm, v(-38.27, -36.03) * mm]});
            skFitSpline(sketch, "E756", {"points": [v(-38.27, -36.03) * mm, v(-38.48, -36.03) * mm, v(-38.76, -35.88) * mm, v(-39.12, -35.6) * mm]});
            skFitSpline(sketch, "E757", {"points": [v(-39.12, -35.6) * mm, v(-39.49, -35.35) * mm, v(-40.07, -34.87) * mm, v(-40.89, -34.14) * mm]});
            skFitSpline(sketch, "E758", {"points": [v(-40.89, -34.14) * mm, v(-40.94, -34.08) * mm, v(-40.98, -34.03) * mm, v(-41, -33.99) * mm]});
            skFitSpline(sketch, "E759", {"points": [v(-41, -33.99) * mm, v(-41.03, -33.95) * mm, v(-41.05, -33.91) * mm, v(-41.06, -33.87) * mm]});
            skFitSpline(sketch, "E760", {"points": [v(-41.06, -33.87) * mm, v(-41.06, -33.85) * mm, v(-41.03, -33.81) * mm, v(-40.97, -33.78) * mm]});
            skFitSpline(sketch, "E761", {"points": [v(-40.97, -33.78) * mm, v(-40.88, -33.78) * mm, v(-40.76, -33.82) * mm, v(-40.63, -33.91) * mm]});
            skFitSpline(sketch, "E762", {"points": [v(-40.63, -33.91) * mm, v(-40.5, -34) * mm, v(-40.37, -34.1) * mm, v(-40.25, -34.18) * mm]});
            skFitSpline(sketch, "E763", {"points": [v(-40.25, -34.18) * mm, v(-40.13, -34.27) * mm, v(-40.03, -34.36) * mm, v(-39.94, -34.45) * mm]});
            skFitSpline(sketch, "E764", {"points": [v(-39.53, -34.75) * mm, v(-39.52, -34.73) * mm, v(-39.5, -34.71) * mm, v(-39.48, -34.68) * mm]});
            skFitSpline(sketch, "E765", {"points": [v(-39.48, -34.68) * mm, v(-39.46, -34.65) * mm, v(-39.45, -34.6) * mm, v(-39.45, -34.51) * mm]});
            skFitSpline(sketch, "E766", {"points": [v(22.3, -54) * mm, v(22.86, -53.32) * mm, v(23.74, -52.78) * mm, v(24.93, -52.38) * mm]});
            skFitSpline(sketch, "E767", {"points": [v(24.93, -52.38) * mm, v(25.54, -52.18) * mm, v(26.1, -52.02) * mm, v(26.63, -51.9) * mm]});
            skFitSpline(sketch, "E768", {"points": [v(26.63, -51.9) * mm, v(27.16, -51.8) * mm, v(27.71, -51.68) * mm, v(28.28, -51.56) * mm]});
            skFitSpline(sketch, "E769", {"points": [v(28.28, -51.56) * mm, v(29.15, -51.37) * mm, v(29.75, -51.17) * mm, v(30.06, -50.94) * mm]});
            skFitSpline(sketch, "E770", {"points": [v(30.06, -50.94) * mm, v(30.37, -50.72) * mm, v(30.53, -50.4) * mm, v(30.53, -49.98) * mm]});
            skFitSpline(sketch, "E771", {"points": [v(30.53, -49.98) * mm, v(30.53, -49.7) * mm, v(30.43, -49.45) * mm, v(30.24, -49.23) * mm]});
            skFitSpline(sketch, "E772", {"points": [v(30.24, -49.23) * mm, v(30.04, -49.02) * mm, v(29.8, -48.86) * mm, v(29.54, -48.75) * mm]});
            skFitSpline(sketch, "E773", {"points": [v(29.54, -48.75) * mm, v(29.23, -48.62) * mm, v(28.91, -48.53) * mm, v(28.58, -48.49) * mm]});
            skFitSpline(sketch, "E774", {"points": [v(28.58, -48.49) * mm, v(28.25, -48.44) * mm, v(27.92, -48.42) * mm, v(27.58, -48.42) * mm]});
            skFitSpline(sketch, "E775", {"points": [v(27.58, -48.42) * mm, v(26.63, -48.42) * mm, v(25.7, -48.6) * mm, v(24.8, -48.94) * mm]});
            skFitSpline(sketch, "E776", {"points": [v(24.8, -48.94) * mm, v(23.88, -49.28) * mm, v(23.11, -49.7) * mm, v(22.49, -50.22) * mm]});
            skFitSpline(sketch, "E777", {"points": [v(22.06, -46.56) * mm, v(22.8, -46.25) * mm, v(23.66, -46) * mm, v(24.66, -45.8) * mm]});
            skFitSpline(sketch, "E778", {"points": [v(24.66, -45.8) * mm, v(25.66, -45.6) * mm, v(26.67, -45.5) * mm, v(27.7, -45.5) * mm]});
            skFitSpline(sketch, "E779", {"points": [v(27.7, -45.5) * mm, v(29.74, -45.5) * mm, v(31.41, -45.96) * mm, v(32.71, -46.9) * mm]});
            skFitSpline(sketch, "E780", {"points": [v(32.71, -46.9) * mm, v(34.01, -47.83) * mm, v(34.66, -49.04) * mm, v(34.66, -50.52) * mm]});
            skFitSpline(sketch, "E781", {"points": [v(34.66, -50.52) * mm, v(34.66, -51.62) * mm, v(34.38, -52.55) * mm, v(33.8, -53.29) * mm]});
            skFitSpline(sketch, "E782", {"points": [v(33.8, -53.29) * mm, v(33.23, -54.03) * mm, v(32.28, -54.62) * mm, v(30.97, -55.06) * mm]});
            skFitSpline(sketch, "E783", {"points": [v(30.97, -55.06) * mm, v(30.4, -55.25) * mm, v(29.79, -55.4) * mm, v(29.13, -55.53) * mm]});
            skFitSpline(sketch, "E784", {"points": [v(29.13, -55.53) * mm, v(28.48, -55.66) * mm, v(27.86, -55.79) * mm, v(27.28, -55.93) * mm]});
            skFitSpline(sketch, "E785", {"points": [v(27.28, -55.93) * mm, v(26.72, -56.07) * mm, v(26.3, -56.26) * mm, v(26, -56.51) * mm]});
            skFitSpline(sketch, "E786", {"points": [v(26, -56.51) * mm, v(25.72, -56.77) * mm, v(25.57, -57.07) * mm, v(25.57, -57.42) * mm]});
            skFitSpline(sketch, "E787", {"points": [v(25.57, -57.42) * mm, v(25.57, -57.8) * mm, v(25.67, -58.08) * mm, v(25.87, -58.27) * mm]});
            skFitSpline(sketch, "E788", {"points": [v(25.87, -58.27) * mm, v(26.07, -58.46) * mm, v(26.32, -58.62) * mm, v(26.63, -58.75) * mm]});
            skFitSpline(sketch, "E789", {"points": [v(26.63, -58.75) * mm, v(26.88, -58.85) * mm, v(27.2, -58.92) * mm, v(27.6, -58.96) * mm]});
            skFitSpline(sketch, "E790", {"points": [v(27.6, -58.96) * mm, v(28, -59) * mm, v(28.32, -59.03) * mm, v(28.56, -59.03) * mm]});
            skFitSpline(sketch, "E791", {"points": [v(28.56, -59.03) * mm, v(29.51, -59.03) * mm, v(30.5, -58.85) * mm, v(31.53, -58.48) * mm]});
            skFitSpline(sketch, "E792", {"points": [v(31.53, -58.48) * mm, v(32.56, -58.12) * mm, v(33.49, -57.6) * mm, v(34.32, -56.92) * mm]});
            skFitSpline(sketch, "E793", {"points": [v(34.76, -60.73) * mm, v(33.92, -61.1) * mm, v(33.02, -61.38) * mm, v(32.06, -61.62) * mm]});
            skFitSpline(sketch, "E794", {"points": [v(32.06, -61.62) * mm, v(31.1, -61.85) * mm, v(29.98, -61.96) * mm, v(28.7, -61.96) * mm]});
            skFitSpline(sketch, "E795", {"points": [v(28.7, -61.96) * mm, v(26.46, -61.96) * mm, v(24.7, -61.47) * mm, v(23.4, -60.5) * mm]});
            skFitSpline(sketch, "E796", {"points": [v(23.4, -60.5) * mm, v(22.1, -59.52) * mm, v(21.44, -58.24) * mm, v(21.44, -56.68) * mm]});
            skFitSpline(sketch, "E797", {"points": [v(21.44, -56.68) * mm, v(21.44, -55.58) * mm, v(21.72, -54.7) * mm, v(22.3, -54) * mm]});
            skSolve(sketch);
        }
        {
            var Q0;
            Q0=qSketchRegion(id+"F0",true);
            extrude(context, id + "F2", {"entities" : qUnion([Q0]), "depth" : 0.8 * mm, "offsetDistance" : 25 * mm, "symmetric" : true});
        }
        {
            var Q0;
            Q0=qSketchRegion(id+"F1",true);
            var Q1;
            Q1=makeQuery(id+"F2.opExtrude","CAP_FACE",FACE,{"disambiguationData":[OSD([sQuery(id+"F0.wireOp",EDGE,"E0.bottom"),sQuery(id+"F0.wireOp",EDGE,"E0.top"),sQuery(id+"F0.wireOp",EDGE,"E0.left"),sQuery(id+"F0.wireOp",EDGE,"E0.right"),sQuery(id+"F0.wireOp",EDGE,"E1"),sQuery(id+"F0.wireOp",EDGE,"E2.filletArc"),sQuery(id+"F0.wireOp",EDGE,"E3.filletArc"),sQuery(id+"F0.wireOp",EDGE,"E4.filletArc"),sQuery(id+"F0.wireOp",EDGE,"E5.filletArc")])],"isStart":true});
            extrude(context, id + "F3", {"entities" : qUnion([Q0]), "operationType" : NewBodyOperationType.REMOVE, "endBound" : BoundingType.UP_TO_SURFACE, "oppositeDirection" : true, "depth" : 25 * mm, "endBoundEntityFace" : qUnion([Q1]), "offsetDistance" : 25 * mm});
        }
        {
            var Q0;
            Q0=qSketchRegion(id+"F1",true);
            var Q1;
            {var subQ27=sQuery(id+"F0.wireOp",EDGE,"E4.filletArc");var subQ29=sQuery(id+"F0.wireOp",EDGE,"E0.left");var subQ31=sQuery(id+"F0.wireOp",EDGE,"E0.top");var subQ32=sQuery(id+"F0.wireOp",EDGE,"E0.right");var subQ33=sQuery(id+"F0.wireOp",EDGE,"E1");var subQ34=sQuery(id+"F0.wireOp",EDGE,"E0.bottom");var subQ37=sQuery(id+"F0.wireOp",EDGE,"E2.filletArc");var subQ39=sQuery(id+"F0.wireOp",EDGE,"E5.filletArc");var subQ40=sQuery(id+"F0.wireOp",EDGE,"E3.filletArc");Q1=makeQuery(id+"F3.boolean.opBoolean","SPLIT",FACE,{"disambiguationData":[TD([makeQuery(id+"F2.opExtrude","SWEPT_FACE",FACE,{"disambiguationData":[OSD([subQ34])]})])],"derivedFrom":makeQuery(id+"F2.opExtrude","CAP_FACE",FACE,{"disambiguationData":[OSD([subQ34,subQ31,subQ29,subQ32,subQ33,subQ37,subQ40,subQ27,subQ39])],"isStart":true})});}
            extrude(context, id + "F4", {"entities" : qUnion([Q0]), "endBound" : BoundingType.UP_TO_SURFACE, "oppositeDirection" : true, "depth" : 25 * mm, "endBoundEntityFace" : qUnion([Q1]), "offsetDistance" : 25 * mm});
        }
        {
            var Q0;
            Q0=makeQuery(id+"F2.opExtrude","CAP_FACE",FACE,{"disambiguationData":[OSD([sQuery(id+"F0.wireOp",EDGE,"E0.bottom"),sQuery(id+"F0.wireOp",EDGE,"E0.top"),sQuery(id+"F0.wireOp",EDGE,"E0.left"),sQuery(id+"F0.wireOp",EDGE,"E0.right"),sQuery(id+"F0.wireOp",EDGE,"E1"),sQuery(id+"F0.wireOp",EDGE,"E2.filletArc"),sQuery(id+"F0.wireOp",EDGE,"E3.filletArc"),sQuery(id+"F0.wireOp",EDGE,"E4.filletArc"),sQuery(id+"F0.wireOp",EDGE,"E5.filletArc"),sQuery(id+"F0.wireOp",EDGE,"E6"),sQuery(id+"F0.wireOp",EDGE,"E7.filletArc"),sQuery(id+"F0.wireOp",EDGE,"E8"),sQuery(id+"F0.wireOp",EDGE,"E9.filletArc")])],"isStart":false});
            var sketch = newSketch(context, id + "F5", { "sketchPlane" : qUnion([Q0])});
            skLineSegment(sketch, "E798", {"start": v(-33.17, -36.58) * mm, "end": v(-34.55, -40.61) * mm});
            skLineSegment(sketch, "E799", {"start": v(-34.55, -40.61) * mm, "end": v(-36.7, -40.61) * mm});
            skLineSegment(sketch, "E800", {"start": v(-36.7, -40.61) * mm, "end": v(-37.17, -41.9) * mm});
            skLineSegment(sketch, "E801", {"start": v(-37.17, -41.9) * mm, "end": v(-35.33, -41.9) * mm});
            skLineSegment(sketch, "E802", {"start": v(-35.33, -41.9) * mm, "end": v(-36.88, -46.4) * mm});
            skLineSegment(sketch, "E803", {"start": v(-36.88, -46.4) * mm, "end": v(-38.8, -46.4) * mm});
            skLineSegment(sketch, "E804", {"start": v(-38.8, -46.4) * mm, "end": v(-41.16, -52.85) * mm});
            skLineSegment(sketch, "E805", {"start": v(-41.16, -52.85) * mm, "end": v(-42.67, -52.85) * mm});
            skLineSegment(sketch, "E806", {"start": v(-42.67, -52.85) * mm, "end": v(-36.54, -36.58) * mm});
            skLineSegment(sketch, "E807", {"start": v(-36.54, -36.58) * mm, "end": v(-33.17, -36.58) * mm});
            skLineSegment(sketch, "E808", {"start": v(-30.36, -40.61) * mm, "end": v(-30.73, -40.61) * mm});
            skLineSegment(sketch, "E809", {"start": v(-32.92, -47.8) * mm, "end": v(-32.53, -47.8) * mm});
            skLineSegment(sketch, "E810", {"start": v(-34.05, -52.85) * mm, "end": v(-34.46, -52.85) * mm});
            skLineSegment(sketch, "E811", {"start": v(-29.5, -36.58) * mm, "end": v(-29.15, -36.58) * mm});
            skLineSegment(sketch, "E812", {"start": v(-25.22, -47.8) * mm, "end": v(-22.4, -47.8) * mm});
            skLineSegment(sketch, "E813", {"start": v(-22.4, -47.8) * mm, "end": v(-23.45, -52.85) * mm});
            skLineSegment(sketch, "E814", {"start": v(-23.45, -52.85) * mm, "end": v(-27.37, -52.85) * mm});
            skLineSegment(sketch, "E815", {"start": v(-27.37, -52.85) * mm, "end": v(-27.44, -49.56) * mm});
            skLineSegment(sketch, "E816", {"start": v(-27.44, -49.56) * mm, "end": v(-28.26, -52.85) * mm});
            skLineSegment(sketch, "E817", {"start": v(-28.26, -52.85) * mm, "end": v(-29.77, -52.85) * mm});
            skLineSegment(sketch, "E818", {"start": v(-29.77, -52.85) * mm, "end": v(-25.48, -36.58) * mm});
            skLineSegment(sketch, "E819", {"start": v(-25.48, -36.58) * mm, "end": v(-23.28, -36.58) * mm});
            skLineSegment(sketch, "E820", {"start": v(-24.53, -41.23) * mm, "end": v(-25.35, -41.23) * mm});
            skLineSegment(sketch, "E821", {"start": v(-25.35, -41.23) * mm, "end": v(-25.89, -43.37) * mm});
            skLineSegment(sketch, "E822", {"start": v(-25.89, -43.37) * mm, "end": v(-25.04, -43.37) * mm});
            skLineSegment(sketch, "E823", {"start": v(-18.75, -44.24) * mm, "end": v(-17.35, -44.24) * mm});
            skLineSegment(sketch, "E824", {"start": v(-17.35, -44.24) * mm, "end": v(-18.8, -52.85) * mm});
            skLineSegment(sketch, "E825", {"start": v(-18.8, -52.85) * mm, "end": v(-20.94, -52.85) * mm});
            skLineSegment(sketch, "E826", {"start": v(-17.9, -36.58) * mm, "end": v(-16.09, -36.58) * mm});
            skLineSegment(sketch, "E827", {"start": v(-16.09, -36.58) * mm, "end": v(-16.77, -40.61) * mm});
            skLineSegment(sketch, "E828", {"start": v(-16.77, -40.61) * mm, "end": v(-18.65, -40.61) * mm});
            skLineSegment(sketch, "E829", {"start": v(-20, -47.8) * mm, "end": v(-19.4, -47.8) * mm});
            skLineSegment(sketch, "E830", {"start": v(-19.4, -47.8) * mm, "end": v(-18.75, -44.24) * mm});
            skLineSegment(sketch, "E831", {"start": v(-12.56, -40.61) * mm, "end": v(-12.93, -40.61) * mm});
            skLineSegment(sketch, "E832", {"start": v(-13.87, -47.8) * mm, "end": v(-13.47, -47.8) * mm});
            skLineSegment(sketch, "E833", {"start": v(-14.11, -52.85) * mm, "end": v(-14.53, -52.85) * mm});
            skLineSegment(sketch, "E834", {"start": v(-12.4, -36.58) * mm, "end": v(-12.05, -36.58) * mm});
            skLineSegment(sketch, "E835", {"start": v(-4.7, -36.58) * mm, "end": v(-4.9, -40.61) * mm});
            skLineSegment(sketch, "E836", {"start": v(-4.9, -40.61) * mm, "end": v(-6.15, -40.61) * mm});
            skLineSegment(sketch, "E837", {"start": v(-6.15, -40.61) * mm, "end": v(-6.94, -52.85) * mm});
            skLineSegment(sketch, "E838", {"start": v(-6.94, -52.85) * mm, "end": v(-8.45, -52.85) * mm});
            skLineSegment(sketch, "E839", {"start": v(-8.45, -52.85) * mm, "end": v(-7.5, -40.61) * mm});
            skLineSegment(sketch, "E840", {"start": v(-7.5, -40.61) * mm, "end": v(-8.74, -40.61) * mm});
            skLineSegment(sketch, "E841", {"start": v(-8.74, -40.61) * mm, "end": v(-8.38, -36.58) * mm});
            skLineSegment(sketch, "E842", {"start": v(-8.38, -36.58) * mm, "end": v(-4.7, -36.58) * mm});
            skLineSegment(sketch, "E843", {"start": v(0.33, -36.58) * mm, "end": v(0.32, -40.61) * mm});
            skLineSegment(sketch, "E844", {"start": v(0.32, -40.61) * mm, "end": v(-0.92, -40.61) * mm});
            skLineSegment(sketch, "E845", {"start": v(-0.92, -40.61) * mm, "end": v(-1.08, -52.85) * mm});
            skLineSegment(sketch, "E846", {"start": v(-1.08, -52.85) * mm, "end": v(-2.59, -52.85) * mm});
            skLineSegment(sketch, "E847", {"start": v(-2.59, -52.85) * mm, "end": v(-2.27, -40.61) * mm});
            skLineSegment(sketch, "E848", {"start": v(-2.27, -40.61) * mm, "end": v(-3.51, -40.61) * mm});
            skLineSegment(sketch, "E849", {"start": v(-3.51, -40.61) * mm, "end": v(-3.36, -36.58) * mm});
            skLineSegment(sketch, "E850", {"start": v(-3.36, -36.58) * mm, "end": v(0.33, -36.58) * mm});
            skLineSegment(sketch, "E851", {"start": v(5.04, -36.58) * mm, "end": v(5.23, -40.61) * mm});
            skLineSegment(sketch, "E852", {"start": v(5.23, -40.61) * mm, "end": v(3.06, -40.61) * mm});
            skLineSegment(sketch, "E853", {"start": v(3.06, -40.61) * mm, "end": v(3.1, -41.9) * mm});
            skLineSegment(sketch, "E854", {"start": v(3.1, -41.9) * mm, "end": v(5.29, -41.9) * mm});
            skLineSegment(sketch, "E855", {"start": v(5.29, -41.9) * mm, "end": v(5.5, -46.4) * mm});
            skLineSegment(sketch, "E856", {"start": v(5.5, -46.4) * mm, "end": v(3.21, -46.4) * mm});
            skLineSegment(sketch, "E857", {"start": v(3.21, -46.4) * mm, "end": v(3.25, -47.8) * mm});
            skLineSegment(sketch, "E858", {"start": v(3.25, -47.8) * mm, "end": v(5.57, -47.8) * mm});
            skLineSegment(sketch, "E859", {"start": v(5.57, -47.8) * mm, "end": v(5.8, -52.85) * mm});
            skLineSegment(sketch, "E860", {"start": v(5.8, -52.85) * mm, "end": v(1.87, -52.85) * mm});
            skLineSegment(sketch, "E861", {"start": v(1.87, -52.85) * mm, "end": v(1.67, -36.58) * mm});
            skLineSegment(sketch, "E862", {"start": v(1.67, -36.58) * mm, "end": v(5.04, -36.58) * mm});
            skLineSegment(sketch, "E863", {"start": v(9.39, -36.58) * mm, "end": v(10.68, -36.58) * mm});
            skLineSegment(sketch, "E864", {"start": v(10.68, -36.58) * mm, "end": v(12.39, -52.85) * mm});
            skLineSegment(sketch, "E865", {"start": v(12.39, -52.85) * mm, "end": v(10.88, -52.85) * mm});
            skLineSegment(sketch, "E866", {"start": v(10.88, -52.85) * mm, "end": v(8.2, -43.76) * mm});
            skLineSegment(sketch, "E867", {"start": v(8.2, -43.76) * mm, "end": v(8.87, -52.85) * mm});
            skLineSegment(sketch, "E868", {"start": v(8.87, -52.85) * mm, "end": v(7.36, -52.85) * mm});
            skLineSegment(sketch, "E869", {"start": v(7.36, -52.85) * mm, "end": v(6.38, -36.58) * mm});
            skLineSegment(sketch, "E870", {"start": v(6.38, -36.58) * mm, "end": v(7.66, -36.58) * mm});
            skLineSegment(sketch, "E871", {"start": v(7.66, -36.58) * mm, "end": v(10.1, -44.41) * mm});
            skLineSegment(sketch, "E872", {"start": v(10.1, -44.41) * mm, "end": v(9.39, -36.58) * mm});
            skLineSegment(sketch, "E873", {"start": v(14.8, -47.8) * mm, "end": v(17.29, -47.8) * mm});
            skLineSegment(sketch, "E874", {"start": v(17.29, -47.8) * mm, "end": v(18.07, -52.85) * mm});
            skLineSegment(sketch, "E875", {"start": v(18.07, -52.85) * mm, "end": v(13.95, -52.85) * mm});
            skLineSegment(sketch, "E876", {"start": v(13.95, -52.85) * mm, "end": v(12.02, -36.58) * mm});
            skLineSegment(sketch, "E877", {"start": v(12.02, -36.58) * mm, "end": v(13.32, -36.58) * mm});
            skLineSegment(sketch, "E878", {"start": v(13.32, -36.58) * mm, "end": v(14.8, -47.8) * mm});
            skLineSegment(sketch, "E879", {"start": v(20.36, -40.61) * mm, "end": v(20, -40.61) * mm});
            skLineSegment(sketch, "E880", {"start": v(21.38, -47.8) * mm, "end": v(21.77, -47.8) * mm});
            skLineSegment(sketch, "E881", {"start": v(22.75, -52.85) * mm, "end": v(22.34, -52.85) * mm});
            skLineSegment(sketch, "E882", {"start": v(19.22, -36.58) * mm, "end": v(19.58, -36.58) * mm});
            skLineSegment(sketch, "E883", {"start": v(29.07, -47.8) * mm, "end": v(31.9, -47.8) * mm});
            skLineSegment(sketch, "E884", {"start": v(31.9, -47.8) * mm, "end": v(33.35, -52.85) * mm});
            skLineSegment(sketch, "E885", {"start": v(33.35, -52.85) * mm, "end": v(29.43, -52.85) * mm});
            skLineSegment(sketch, "E886", {"start": v(29.43, -52.85) * mm, "end": v(27.73, -49.56) * mm});
            skLineSegment(sketch, "E887", {"start": v(27.73, -49.56) * mm, "end": v(28.54, -52.85) * mm});
            skLineSegment(sketch, "E888", {"start": v(28.54, -52.85) * mm, "end": v(27.03, -52.85) * mm});
            skLineSegment(sketch, "E889", {"start": v(27.03, -52.85) * mm, "end": v(23.24, -36.58) * mm});
            skLineSegment(sketch, "E890", {"start": v(23.24, -36.58) * mm, "end": v(25.44, -36.58) * mm});
            skLineSegment(sketch, "E891", {"start": v(26.5, -41.23) * mm, "end": v(25.68, -41.23) * mm});
            skLineSegment(sketch, "E892", {"start": v(25.68, -41.23) * mm, "end": v(26.2, -43.37) * mm});
            skLineSegment(sketch, "E893", {"start": v(26.2, -43.37) * mm, "end": v(27.05, -43.37) * mm});
            skLineSegment(sketch, "E894", {"start": v(31.77, -40.61) * mm, "end": v(31, -40.61) * mm});
            skLineSegment(sketch, "E895", {"start": v(31, -40.61) * mm, "end": v(33.15, -47.8) * mm});
            skLineSegment(sketch, "E896", {"start": v(33.15, -47.8) * mm, "end": v(33.98, -47.8) * mm});
            skLineSegment(sketch, "E897", {"start": v(35.53, -52.85) * mm, "end": v(33.15, -52.85) * mm});
            skLineSegment(sketch, "E898", {"start": v(33.15, -52.85) * mm, "end": v(28.5, -36.58) * mm});
            skLineSegment(sketch, "E899", {"start": v(28.5, -36.58) * mm, "end": v(30.53, -36.58) * mm});
            skLineSegment(sketch, "E900", {"start": v(42.25, -52.85) * mm, "end": v(39.46, -52.85) * mm});
            skLineSegment(sketch, "E901", {"start": v(39.46, -52.85) * mm, "end": v(37.74, -47.8) * mm});
            skLineSegment(sketch, "E902", {"start": v(37.74, -47.8) * mm, "end": v(40, -47.8) * mm});
            skLineSegment(sketch, "E903", {"start": v(40, -47.8) * mm, "end": v(36.4, -42.28) * mm});
            skLineSegment(sketch, "E904", {"start": v(35.33, -36.58) * mm, "end": v(37.6, -36.58) * mm});
            skLineSegment(sketch, "E905", {"start": v(37.6, -36.58) * mm, "end": v(39.13, -40.61) * mm});
            skLineSegment(sketch, "E906", {"start": v(39.13, -40.61) * mm, "end": v(37.14, -40.61) * mm});
            skFitSpline(sketch, "E907", {"points": [v(-38.46, 24.44) * mm, v(-13.13, 15.5) * mm, v(12.14, 6.58) * mm, v(37.42, -2.34) * mm]});
            skFitSpline(sketch, "E908", {"points": [v(37.42, -2.34) * mm, v(37.37, -2.84) * mm, v(37.14, -3.24) * mm, v(36.96, -3.65) * mm]});
            skFitSpline(sketch, "E909", {"points": [v(36.96, -3.65) * mm, v(36.18, -5.4) * mm, v(35.35, -7.13) * mm, v(34.26, -8.8) * mm]});
            skFitSpline(sketch, "E910", {"points": [v(34.26, -8.8) * mm, v(30.07, -7.33) * mm, v(25.9, -5.85) * mm, v(21.66, -4.36) * mm]});
            skFitSpline(sketch, "E911", {"points": [v(21.66, -4.36) * mm, v(21.33, -5.29) * mm, v(21.02, -6.15) * mm, v(20.69, -7.1) * mm]});
            skFitSpline(sketch, "E912", {"points": [v(20.69, -7.1) * mm, v(22.46, -7.72) * mm, v(24.22, -8.34) * mm, v(26.02, -8.98) * mm]});
            skFitSpline(sketch, "E913", {"points": [v(26.02, -8.98) * mm, v(25.7, -9.9) * mm, v(25.4, -10.74) * mm, v(25.07, -11.67) * mm]});
            skFitSpline(sketch, "E914", {"points": [v(25.07, -11.67) * mm, v(21.47, -10.4) * mm, v(17.9, -9.14) * mm, v(14.26, -7.85) * mm]});
            skFitSpline(sketch, "E915", {"points": [v(14.26, -7.85) * mm, v(13.94, -8.78) * mm, v(13.64, -9.63) * mm, v(13.31, -10.55) * mm]});
            skFitSpline(sketch, "E916", {"points": [v(13.31, -10.55) * mm, v(11.48, -9.9) * mm, v(9.73, -9.29) * mm, v(7.91, -8.64) * mm]});
            skFitSpline(sketch, "E917", {"points": [v(7.91, -8.64) * mm, v(7.58, -9.58) * mm, v(7.27, -10.45) * mm, v(6.94, -11.4) * mm]});
            skFitSpline(sketch, "E918", {"points": [v(6.94, -11.4) * mm, v(9.6, -12.34) * mm, v(12.25, -13.28) * mm, v(15, -14.25) * mm]});
            skFitSpline(sketch, "E919", {"points": [v(15, -14.25) * mm, v(14.67, -15.17) * mm, v(14.38, -16.01) * mm, v(14.04, -16.97) * mm]});
            skFitSpline(sketch, "E920", {"points": [v(14.04, -16.97) * mm, v(15.89, -17.63) * mm, v(17.66, -18.25) * mm, v(19.47, -18.9) * mm]});
            skFitSpline(sketch, "E921", {"points": [v(19.47, -18.9) * mm, v(19.14, -19.83) * mm, v(18.85, -20.65) * mm, v(18.53, -21.56) * mm]});
            skFitSpline(sketch, "E922", {"points": [v(18.53, -21.56) * mm, v(17.67, -21.26) * mm, v(16.82, -20.96) * mm, v(15.87, -20.62) * mm]});
            skFitSpline(sketch, "E923", {"points": [v(15.87, -20.62) * mm, v(15.54, -21.57) * mm, v(15.23, -22.44) * mm, v(14.9, -23.38) * mm]});
            skFitSpline(sketch, "E924", {"points": [v(14.9, -23.38) * mm, v(12.13, -22.4) * mm, v(9.47, -21.47) * mm, v(6.73, -20.5) * mm]});
            skFitSpline(sketch, "E925", {"points": [v(6.73, -20.5) * mm, v(6.4, -21.43) * mm, v(6.1, -22.28) * mm, v(5.78, -23.2) * mm]});
            skFitSpline(sketch, "E926", {"points": [v(5.78, -23.2) * mm, v(4.85, -22.87) * mm, v(4, -22.57) * mm, v(3.06, -22.24) * mm]});
            skFitSpline(sketch, "E927", {"points": [v(3.06, -22.24) * mm, v(2.74, -23.16) * mm, v(2.44, -24) * mm, v(2.1, -24.96) * mm]});
            skFitSpline(sketch, "E928", {"points": [v(2.1, -24.96) * mm, v(-0.66, -23.98) * mm, v(-3.34, -23.03) * mm, v(-6.05, -22.08) * mm]});
            skFitSpline(sketch, "E929", {"points": [v(-6.05, -22.08) * mm, v(-6.4, -23.04) * mm, v(-6.7, -23.89) * mm, v(-7, -24.78) * mm]});
            skFitSpline(sketch, "E930", {"points": [v(-7, -24.78) * mm, v(-6.21, -25.26) * mm, v(-5.28, -25.38) * mm, v(-4.44, -25.81) * mm]});
            skFitSpline(sketch, "E931", {"points": [v(-4.44, -25.81) * mm, v(-4.48, -26.43) * mm, v(-4.76, -26.96) * mm, v(-4.98, -27.51) * mm]});
            skFitSpline(sketch, "E932", {"points": [v(-4.98, -27.51) * mm, v(-28.85, -25) * mm, v(-46.2, -0.28) * mm, v(-38.46, 24.44) * mm]});
            skFitSpline(sketch, "E933", {"points": [v(-3.14, 47.2) * mm, v(-9.1, 49.27) * mm, v(-15.64, 46.11) * mm, v(-17.78, 40.13) * mm]});
            skFitSpline(sketch, "E934", {"points": [v(-17.78, 40.13) * mm, v(-19.92, 34.13) * mm, v(-16.72, 27.5) * mm, v(-10.66, 25.38) * mm]});
            skFitSpline(sketch, "E935", {"points": [v(-10.66, 25.38) * mm, v(-4.65, 23.28) * mm, v(1.91, 26.46) * mm, v(4.01, 32.48) * mm]});
            skFitSpline(sketch, "E936", {"points": [v(4.01, 32.48) * mm, v(6.13, 38.54) * mm, v(2.95, 45.08) * mm, v(-3.14, 47.2) * mm]});
            skFitSpline(sketch, "E937", {"points": [v(26.9, 36.7) * mm, v(25.9, 36.86) * mm, v(25.1, 37.37) * mm, v(24.17, 37.5) * mm]});
            skFitSpline(sketch, "E938", {"points": [v(24.17, 37.5) * mm, v(23.86, 36.62) * mm, v(23.56, 35.77) * mm, v(23.22, 34.82) * mm]});
            skFitSpline(sketch, "E939", {"points": [v(23.22, 34.82) * mm, v(25.03, 34.18) * mm, v(26.8, 33.55) * mm, v(28.59, 32.92) * mm]});
            skFitSpline(sketch, "E940", {"points": [v(28.59, 32.92) * mm, v(28.26, 32) * mm, v(27.97, 31.17) * mm, v(27.65, 30.26) * mm]});
            skFitSpline(sketch, "E941", {"points": [v(27.65, 30.26) * mm, v(26.77, 30.57) * mm, v(25.92, 30.87) * mm, v(25.04, 31.18) * mm]});
            skFitSpline(sketch, "E942", {"points": [v(25.04, 31.18) * mm, v(24.56, 30.3) * mm, v(24.36, 29.39) * mm, v(24, 28.45) * mm]});
            skFitSpline(sketch, "E943", {"points": [v(24, 28.45) * mm, v(25.83, 27.8) * mm, v(27.58, 27.18) * mm, v(29.42, 26.53) * mm]});
            skFitSpline(sketch, "E944", {"points": [v(29.42, 26.53) * mm, v(29.09, 25.6) * mm, v(28.8, 24.76) * mm, v(28.46, 23.84) * mm]});
            skFitSpline(sketch, "E945", {"points": [v(28.46, 23.84) * mm, v(29.4, 23.51) * mm, v(30.24, 23.21) * mm, v(31.14, 22.9) * mm]});
            skFitSpline(sketch, "E946", {"points": [v(31.14, 22.9) * mm, v(30.82, 21.97) * mm, v(30.52, 21.13) * mm, v(30.2, 20.2) * mm]});
            skFitSpline(sketch, "E947", {"points": [v(30.2, 20.2) * mm, v(27.54, 21.14) * mm, v(24.88, 22.08) * mm, v(22.14, 23.04) * mm]});
            skFitSpline(sketch, "E948", {"points": [v(22.14, 23.04) * mm, v(21.72, 22.13) * mm, v(21.45, 21.25) * mm, v(21.15, 20.3) * mm]});
            skFitSpline(sketch, "E949", {"points": [v(21.15, 20.3) * mm, v(24.75, 19.02) * mm, v(28.32, 17.76) * mm, v(31.94, 16.48) * mm]});
            skFitSpline(sketch, "E950", {"points": [v(31.94, 16.48) * mm, v(31.62, 15.56) * mm, v(31.32, 14.72) * mm, v(31, 13.79) * mm]});
            skFitSpline(sketch, "E951", {"points": [v(31, 13.79) * mm, v(29.23, 14.41) * mm, v(27.48, 15.03) * mm, v(25.67, 15.67) * mm]});
            skFitSpline(sketch, "E952", {"points": [v(25.67, 15.67) * mm, v(25.33, 14.72) * mm, v(25.03, 13.86) * mm, v(24.7, 12.92) * mm]});
            skFitSpline(sketch, "E953", {"points": [v(24.7, 12.92) * mm, v(29.8, 11.12) * mm, v(34.88, 9.33) * mm, v(40.01, 7.52) * mm]});
            skFitSpline(sketch, "E954", {"points": [v(40.01, 7.52) * mm, v(39.75, 5.09) * mm, v(39.2, 2.8) * mm, v(38.48, 0.47) * mm]});
            skFitSpline(sketch, "E955", {"points": [v(38.48, 0.47) * mm, v(13.16, 9.4) * mm, v(-12.12, 18.33) * mm, v(-37.47, 27.28) * mm]});
            skFitSpline(sketch, "E956", {"points": [v(-37.47, 27.28) * mm, v(-36.88, 28.88) * mm, v(-36.17, 30.4) * mm, v(-35.34, 31.85) * mm]});
            skFitSpline(sketch, "E957", {"points": [v(-35.34, 31.85) * mm, v(-29.14, 42.7) * mm, v(-19.95, 49.52) * mm, v(-7.7, 52.04) * mm]});
            skFitSpline(sketch, "E958", {"points": [v(-7.7, 52.04) * mm, v(1.08, 53.84) * mm, v(9.54, 52.6) * mm, v(17.6, 48.75) * mm]});
            skFitSpline(sketch, "E959", {"points": [v(17.6, 48.75) * mm, v(21.42, 46.93) * mm, v(24.83, 44.5) * mm, v(27.89, 41.6) * mm]});
            skFitSpline(sketch, "E960", {"points": [v(27.89, 41.6) * mm, v(28.32, 41.18) * mm, v(28.4, 40.84) * mm, v(28.19, 40.28) * mm]});
            skFitSpline(sketch, "E961", {"points": [v(28.19, 40.28) * mm, v(27.72, 39.12) * mm, v(27.34, 37.93) * mm, v(26.9, 36.7) * mm]});
            skFitSpline(sketch, "E962", {"points": [v(-32.53, -47.8) * mm, v(-32.2, -47.8) * mm, v(-31.83, -47.43) * mm, v(-31.38, -46.7) * mm]});
            skFitSpline(sketch, "E963", {"points": [v(-31.38, -46.7) * mm, v(-30.95, -45.97) * mm, v(-30.58, -45.1) * mm, v(-30.29, -44.09) * mm]});
            skFitSpline(sketch, "E964", {"points": [v(-30.29, -44.09) * mm, v(-30, -43.1) * mm, v(-29.87, -42.27) * mm, v(-29.88, -41.6) * mm]});
            skFitSpline(sketch, "E965", {"points": [v(-29.88, -41.6) * mm, v(-29.9, -40.94) * mm, v(-30.06, -40.61) * mm, v(-30.36, -40.61) * mm]});
            skFitSpline(sketch, "E966", {"points": [v(-30.73, -40.61) * mm, v(-31.03, -40.61) * mm, v(-31.39, -40.94) * mm, v(-31.8, -41.6) * mm]});
            skFitSpline(sketch, "E967", {"points": [v(-31.8, -41.6) * mm, v(-32.23, -42.27) * mm, v(-32.6, -43.1) * mm, v(-32.9, -44.09) * mm]});
            skFitSpline(sketch, "E968", {"points": [v(-32.9, -44.09) * mm, v(-33.22, -45.1) * mm, v(-33.39, -45.97) * mm, v(-33.4, -46.7) * mm]});
            skFitSpline(sketch, "E969", {"points": [v(-33.4, -46.7) * mm, v(-33.4, -47.43) * mm, v(-33.24, -47.8) * mm, v(-32.92, -47.8) * mm]});
            skFitSpline(sketch, "E970", {"points": [v(-29.15, -36.58) * mm, v(-28.5, -36.58) * mm, v(-28.15, -37.27) * mm, v(-28.1, -38.67) * mm]});
            skFitSpline(sketch, "E971", {"points": [v(-28.1, -38.67) * mm, v(-28.03, -40.1) * mm, v(-28.3, -41.9) * mm, v(-28.9, -44.09) * mm]});
            skFitSpline(sketch, "E972", {"points": [v(-28.9, -44.09) * mm, v(-29.53, -46.37) * mm, v(-30.35, -48.4) * mm, v(-31.35, -50.14) * mm]});
            skFitSpline(sketch, "E973", {"points": [v(-31.35, -50.14) * mm, v(-32.39, -51.93) * mm, v(-33.3, -52.85) * mm, v(-34.05, -52.85) * mm]});
            skFitSpline(sketch, "E974", {"points": [v(-34.46, -52.85) * mm, v(-35.21, -52.85) * mm, v(-35.56, -51.93) * mm, v(-35.5, -50.14) * mm]});
            skFitSpline(sketch, "E975", {"points": [v(-35.5, -50.14) * mm, v(-35.46, -48.4) * mm, v(-35.05, -46.37) * mm, v(-34.3, -44.09) * mm]});
            skFitSpline(sketch, "E976", {"points": [v(-34.3, -44.09) * mm, v(-33.58, -41.9) * mm, v(-32.75, -40.1) * mm, v(-31.82, -38.67) * mm]});
            skFitSpline(sketch, "E977", {"points": [v(-31.82, -38.67) * mm, v(-30.91, -37.27) * mm, v(-30.14, -36.58) * mm, v(-29.5, -36.58) * mm]});
            skFitSpline(sketch, "E978", {"points": [v(-22.8, -42.06) * mm, v(-23.06, -43.24) * mm, v(-23.4, -44.33) * mm, v(-23.84, -45.35) * mm]});
            skFitSpline(sketch, "E979", {"points": [v(-23.84, -45.35) * mm, v(-24.28, -46.36) * mm, v(-24.74, -47.18) * mm, v(-25.22, -47.8) * mm]});
            skFitSpline(sketch, "E980", {"points": [v(-23.28, -36.58) * mm, v(-22.8, -36.6) * mm, v(-22.52, -37.11) * mm, v(-22.42, -38.15) * mm]});
            skFitSpline(sketch, "E981", {"points": [v(-22.42, -38.15) * mm, v(-22.32, -39.2) * mm, v(-22.44, -40.5) * mm, v(-22.8, -42.06) * mm]});
            skFitSpline(sketch, "E982", {"points": [v(-25.04, -43.37) * mm, v(-24.95, -43.37) * mm, v(-24.84, -43.26) * mm, v(-24.73, -43.05) * mm]});
            skFitSpline(sketch, "E983", {"points": [v(-24.73, -43.05) * mm, v(-24.6, -42.84) * mm, v(-24.52, -42.58) * mm, v(-24.45, -42.29) * mm]});
            skFitSpline(sketch, "E984", {"points": [v(-24.45, -42.29) * mm, v(-24.37, -42) * mm, v(-24.35, -41.75) * mm, v(-24.36, -41.54) * mm]});
            skFitSpline(sketch, "E985", {"points": [v(-24.36, -41.54) * mm, v(-24.38, -41.33) * mm, v(-24.43, -41.23) * mm, v(-24.53, -41.23) * mm]});
            skFitSpline(sketch, "E986", {"points": [v(-20.94, -52.85) * mm, v(-21.69, -52.85) * mm, v(-22.15, -51.93) * mm, v(-22.3, -50.14) * mm]});
            skFitSpline(sketch, "E987", {"points": [v(-22.3, -50.14) * mm, v(-22.46, -48.4) * mm, v(-22.29, -46.37) * mm, v(-21.8, -44.09) * mm]});
            skFitSpline(sketch, "E988", {"points": [v(-21.8, -44.09) * mm, v(-21.35, -41.9) * mm, v(-20.73, -40.1) * mm, v(-19.97, -38.67) * mm]});
            skFitSpline(sketch, "E989", {"points": [v(-19.97, -38.67) * mm, v(-19.23, -37.27) * mm, v(-18.54, -36.58) * mm, v(-17.9, -36.58) * mm]});
            skFitSpline(sketch, "E990", {"points": [v(-18.65, -40.61) * mm, v(-18.95, -40.61) * mm, v(-19.27, -40.94) * mm, v(-19.61, -41.6) * mm]});
            skFitSpline(sketch, "E991", {"points": [v(-19.61, -41.6) * mm, v(-19.95, -42.27) * mm, v(-20.22, -43.1) * mm, v(-20.42, -44.09) * mm]});
            skFitSpline(sketch, "E992", {"points": [v(-20.42, -44.09) * mm, v(-20.62, -45.1) * mm, v(-20.68, -45.97) * mm, v(-20.6, -46.7) * mm]});
            skFitSpline(sketch, "E993", {"points": [v(-20.6, -46.7) * mm, v(-20.51, -47.43) * mm, v(-20.31, -47.8) * mm, v(-20, -47.8) * mm]});
            skFitSpline(sketch, "E994", {"points": [v(-13.47, -47.8) * mm, v(-13.15, -47.8) * mm, v(-12.84, -47.43) * mm, v(-12.52, -46.7) * mm]});
            skFitSpline(sketch, "E995", {"points": [v(-12.52, -46.7) * mm, v(-12.21, -45.97) * mm, v(-12, -45.1) * mm, v(-11.88, -44.09) * mm]});
            skFitSpline(sketch, "E996", {"points": [v(-11.88, -44.09) * mm, v(-11.77, -43.1) * mm, v(-11.78, -42.27) * mm, v(-11.9, -41.6) * mm]});
            skFitSpline(sketch, "E997", {"points": [v(-11.9, -41.6) * mm, v(-12.04, -40.94) * mm, v(-12.26, -40.61) * mm, v(-12.56, -40.61) * mm]});
            skFitSpline(sketch, "E998", {"points": [v(-12.93, -40.61) * mm, v(-13.23, -40.61) * mm, v(-13.53, -40.94) * mm, v(-13.83, -41.6) * mm]});
            skFitSpline(sketch, "E999", {"points": [v(-13.83, -41.6) * mm, v(-14.14, -42.27) * mm, v(-14.36, -43.1) * mm, v(-14.5, -44.09) * mm]});
            skFitSpline(sketch, "E1000", {"points": [v(-14.5, -44.09) * mm, v(-14.64, -45.1) * mm, v(-14.65, -45.97) * mm, v(-14.53, -46.7) * mm]});
            skFitSpline(sketch, "E1001", {"points": [v(-14.53, -46.7) * mm, v(-14.4, -47.43) * mm, v(-14.19, -47.8) * mm, v(-13.87, -47.8) * mm]});
            skFitSpline(sketch, "E1002", {"points": [v(-12.05, -36.58) * mm, v(-11.4, -36.58) * mm, v(-10.93, -37.27) * mm, v(-10.63, -38.67) * mm]});
            skFitSpline(sketch, "E1003", {"points": [v(-10.63, -38.67) * mm, v(-10.32, -40.1) * mm, v(-10.27, -41.9) * mm, v(-10.5, -44.09) * mm]});
            skFitSpline(sketch, "E1004", {"points": [v(-10.5, -44.09) * mm, v(-10.73, -46.37) * mm, v(-11.2, -48.4) * mm, v(-11.9, -50.14) * mm]});
            skFitSpline(sketch, "E1005", {"points": [v(-11.9, -50.14) * mm, v(-12.62, -51.93) * mm, v(-13.36, -52.85) * mm, v(-14.11, -52.85) * mm]});
            skFitSpline(sketch, "E1006", {"points": [v(-14.53, -52.85) * mm, v(-15.28, -52.85) * mm, v(-15.79, -51.93) * mm, v(-16.05, -50.14) * mm]});
            skFitSpline(sketch, "E1007", {"points": [v(-16.05, -50.14) * mm, v(-16.3, -48.4) * mm, v(-16.24, -46.37) * mm, v(-15.89, -44.09) * mm]});
            skFitSpline(sketch, "E1008", {"points": [v(-15.89, -44.09) * mm, v(-15.55, -41.9) * mm, v(-15.04, -40.1) * mm, v(-14.36, -38.67) * mm]});
            skFitSpline(sketch, "E1009", {"points": [v(-14.36, -38.67) * mm, v(-13.7, -37.27) * mm, v(-13.05, -36.58) * mm, v(-12.4, -36.58) * mm]});
            skFitSpline(sketch, "E1010", {"points": [v(21.77, -47.8) * mm, v(22.09, -47.8) * mm, v(22.29, -47.43) * mm, v(22.36, -46.7) * mm]});
            skFitSpline(sketch, "E1011", {"points": [v(22.36, -46.7) * mm, v(22.43, -45.97) * mm, v(22.37, -45.1) * mm, v(22.16, -44.09) * mm]});
            skFitSpline(sketch, "E1012", {"points": [v(22.16, -44.09) * mm, v(21.96, -43.1) * mm, v(21.68, -42.27) * mm, v(21.33, -41.6) * mm]});
            skFitSpline(sketch, "E1013", {"points": [v(21.33, -41.6) * mm, v(20.99, -40.94) * mm, v(20.67, -40.61) * mm, v(20.36, -40.61) * mm]});
            skFitSpline(sketch, "E1014", {"points": [v(20, -40.61) * mm, v(19.7, -40.61) * mm, v(19.5, -40.94) * mm, v(19.4, -41.6) * mm]});
            skFitSpline(sketch, "E1015", {"points": [v(19.4, -41.6) * mm, v(19.32, -42.27) * mm, v(19.37, -43.1) * mm, v(19.54, -44.09) * mm]});
            skFitSpline(sketch, "E1016", {"points": [v(19.54, -44.09) * mm, v(19.73, -45.1) * mm, v(20, -45.97) * mm, v(20.35, -46.7) * mm]});
            skFitSpline(sketch, "E1017", {"points": [v(20.35, -46.7) * mm, v(20.71, -47.43) * mm, v(21.06, -47.8) * mm, v(21.38, -47.8) * mm]});
            skFitSpline(sketch, "E1018", {"points": [v(19.58, -36.58) * mm, v(20.22, -36.58) * mm, v(20.91, -37.27) * mm, v(21.67, -38.67) * mm]});
            skFitSpline(sketch, "E1019", {"points": [v(21.67, -38.67) * mm, v(22.44, -40.1) * mm, v(23.07, -41.9) * mm, v(23.55, -44.09) * mm]});
            skFitSpline(sketch, "E1020", {"points": [v(23.55, -44.09) * mm, v(24.05, -46.37) * mm, v(24.24, -48.4) * mm, v(24.1, -50.14) * mm]});
            skFitSpline(sketch, "E1021", {"points": [v(24.1, -50.14) * mm, v(23.96, -51.93) * mm, v(23.5, -52.85) * mm, v(22.75, -52.85) * mm]});
            skFitSpline(sketch, "E1022", {"points": [v(22.34, -52.85) * mm, v(21.6, -52.85) * mm, v(20.79, -51.93) * mm, v(19.95, -50.14) * mm]});
            skFitSpline(sketch, "E1023", {"points": [v(19.95, -50.14) * mm, v(19.13, -48.4) * mm, v(18.54, -46.37) * mm, v(18.15, -44.09) * mm]});
            skFitSpline(sketch, "E1024", {"points": [v(18.15, -44.09) * mm, v(17.79, -41.9) * mm, v(17.72, -40.1) * mm, v(17.94, -38.67) * mm]});
            skFitSpline(sketch, "E1025", {"points": [v(17.94, -38.67) * mm, v(18.15, -37.27) * mm, v(18.58, -36.58) * mm, v(19.22, -36.58) * mm]});
            skFitSpline(sketch, "E1026", {"points": [v(28.65, -42.06) * mm, v(28.97, -43.24) * mm, v(29.17, -44.33) * mm, v(29.24, -45.35) * mm]});
            skFitSpline(sketch, "E1027", {"points": [v(29.24, -45.35) * mm, v(29.3, -46.36) * mm, v(29.25, -47.18) * mm, v(29.07, -47.8) * mm]});
            skFitSpline(sketch, "E1028", {"points": [v(25.44, -36.58) * mm, v(25.92, -36.6) * mm, v(26.46, -37.11) * mm, v(27.07, -38.15) * mm]});
            skFitSpline(sketch, "E1029", {"points": [v(27.07, -38.15) * mm, v(27.7, -39.2) * mm, v(28.22, -40.5) * mm, v(28.65, -42.06) * mm]});
            skFitSpline(sketch, "E1030", {"points": [v(27.05, -43.37) * mm, v(27.14, -43.37) * mm, v(27.2, -43.26) * mm, v(27.2, -43.05) * mm]});
            skFitSpline(sketch, "E1031", {"points": [v(27.2, -43.05) * mm, v(27.22, -42.84) * mm, v(27.19, -42.58) * mm, v(27.11, -42.29) * mm]});
            skFitSpline(sketch, "E1032", {"points": [v(27.11, -42.29) * mm, v(27.04, -42) * mm, v(26.94, -41.75) * mm, v(26.82, -41.54) * mm]});
            skFitSpline(sketch, "E1033", {"points": [v(26.82, -41.54) * mm, v(26.7, -41.33) * mm, v(26.6, -41.23) * mm, v(26.5, -41.23) * mm]});
            skFitSpline(sketch, "E1034", {"points": [v(33.98, -47.8) * mm, v(34.3, -47.8) * mm, v(34.45, -47.43) * mm, v(34.44, -46.7) * mm]});
            skFitSpline(sketch, "E1035", {"points": [v(34.44, -46.7) * mm, v(34.44, -45.97) * mm, v(34.27, -45.1) * mm, v(33.95, -44.09) * mm]});
            skFitSpline(sketch, "E1036", {"points": [v(33.95, -44.09) * mm, v(33.64, -43.1) * mm, v(33.27, -42.27) * mm, v(32.85, -41.6) * mm]});
            skFitSpline(sketch, "E1037", {"points": [v(32.85, -41.6) * mm, v(32.43, -40.94) * mm, v(32.07, -40.61) * mm, v(31.77, -40.61) * mm]});
            skFitSpline(sketch, "E1038", {"points": [v(30.53, -36.58) * mm, v(31.17, -36.58) * mm, v(31.94, -37.27) * mm, v(32.85, -38.67) * mm]});
            skFitSpline(sketch, "E1039", {"points": [v(32.85, -38.67) * mm, v(33.8, -40.1) * mm, v(34.62, -41.9) * mm, v(35.34, -44.09) * mm]});
            skFitSpline(sketch, "E1040", {"points": [v(35.34, -44.09) * mm, v(36.1, -46.37) * mm, v(36.52, -48.4) * mm, v(36.57, -50.14) * mm]});
            skFitSpline(sketch, "E1041", {"points": [v(36.57, -50.14) * mm, v(36.62, -51.93) * mm, v(36.27, -52.85) * mm, v(35.53, -52.85) * mm]});
            skFitSpline(sketch, "E1042", {"points": [v(37.14, -40.61) * mm, v(37.17, -40.65) * mm, v(38.33, -42.39) * mm, v(40.73, -45.98) * mm]});
            skFitSpline(sketch, "E1043", {"points": [v(40.73, -45.98) * mm, v(41.15, -46.7) * mm, v(41.51, -47.48) * mm, v(41.82, -48.3) * mm]});
            skFitSpline(sketch, "E1044", {"points": [v(41.82, -48.3) * mm, v(42.27, -49.49) * mm, v(42.54, -50.54) * mm, v(42.64, -51.45) * mm]});
            skFitSpline(sketch, "E1045", {"points": [v(42.64, -51.45) * mm, v(42.73, -52.38) * mm, v(42.6, -52.85) * mm, v(42.25, -52.85) * mm]});
            skFitSpline(sketch, "E1046", {"points": [v(36.4, -42.28) * mm, v(36.07, -41.72) * mm, v(35.75, -41.02) * mm, v(35.47, -40.2) * mm]});
            skFitSpline(sketch, "E1047", {"points": [v(35.47, -40.2) * mm, v(35.12, -39.2) * mm, v(34.94, -38.34) * mm, v(34.91, -37.63) * mm]});
            skFitSpline(sketch, "E1048", {"points": [v(34.91, -37.63) * mm, v(34.88, -36.93) * mm, v(35.02, -36.58) * mm, v(35.33, -36.58) * mm]});
            skSolve(sketch);
        }
        {
            var Q0;
            Q0 = qSketchRegion(id + "F5", true);
            extrude(context, id + "F6", {"entities" : qUnion([Q0]), "operationType" : NewBodyOperationType.ADD, "depth" : 1 * mm, "offsetDistance" : 25 * mm});
        }
    });
